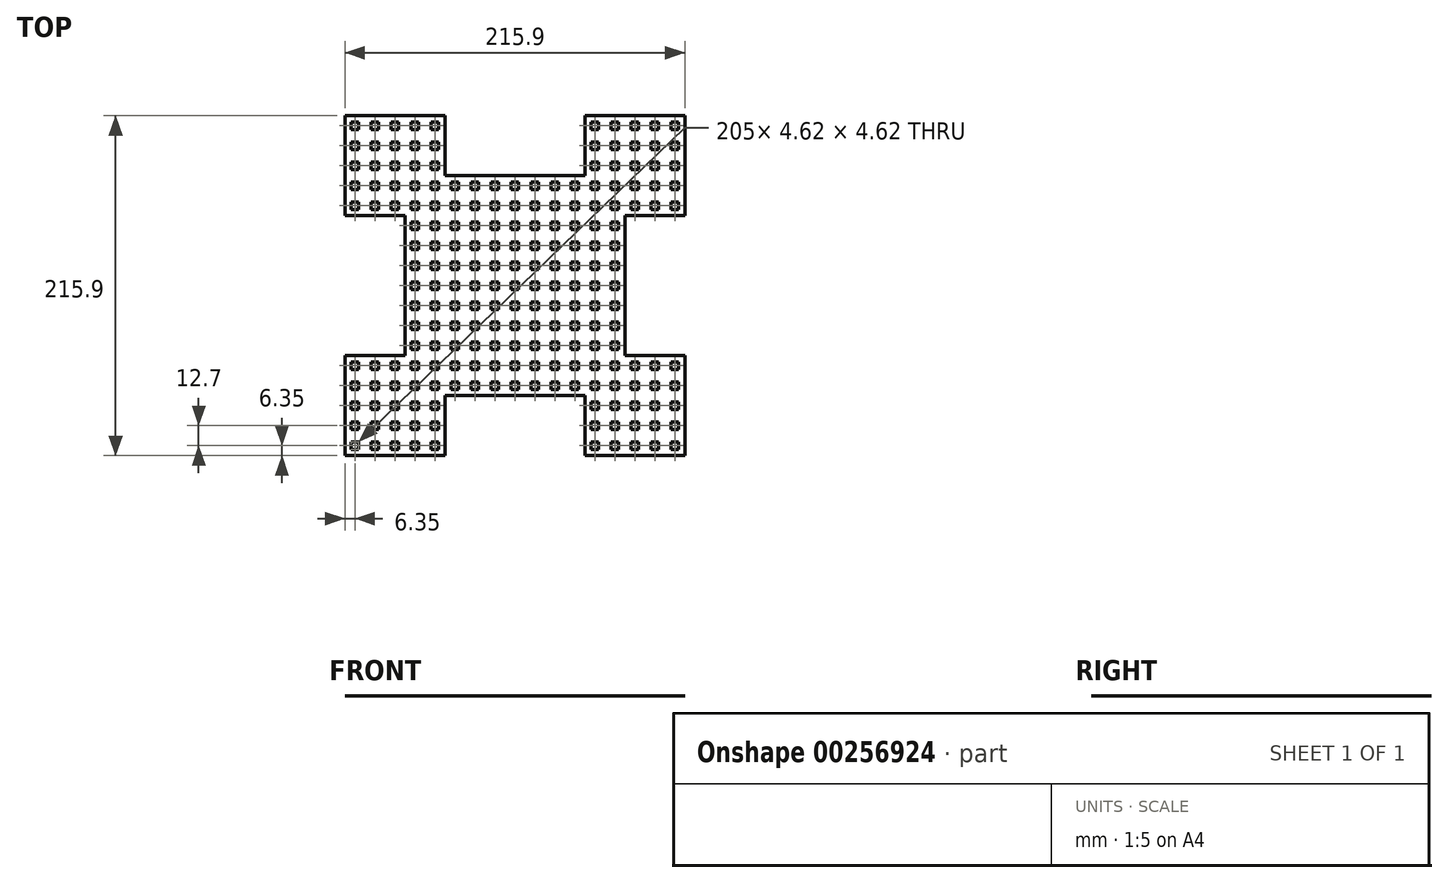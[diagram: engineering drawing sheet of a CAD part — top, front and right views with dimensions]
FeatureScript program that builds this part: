
annotation { "Feature Type Name" : "Feature", "Feature Type Description" : "" }
export const myFeature = defineFeature(function(context is Context, id is Id, definition is map)
    precondition{}
    {
        {
            var Q0;
            Q0=qCreatedBy(makeId("Top.planeOp"),FACE);
            var sketch = newSketch(context, id + "F0", { "sketchPlane" : qUnion([Q0])});
            skLineSegment(sketch, "E0.bottom", {"start": v(101.6, 101.6) * mm, "end": v(50.8, 101.6) * mm});
            skLineSegment(sketch, "E0.right", {"start": v(-101.6, 101.6) * mm, "end": v(-101.6, 95.25) * mm});
            skPoint(sketch, "E0.middle", {"position": v(0, 0) * mm});
            skLineSegment(sketch, "E1.bottom", {"start": v(-101.6, 101.6) * mm, "end": v(-95.25, 101.6) * mm});
            skLineSegment(sketch, "E2.bottom", {"start": v(-97.56, 97.56) * mm, "end": v(-92.94, 97.56) * mm});
            skLineSegment(sketch, "E2.top", {"start": v(-97.56, 92.94) * mm, "end": v(-92.94, 92.94) * mm});
            skLineSegment(sketch, "E2.left", {"start": v(-97.56, 97.56) * mm, "end": v(-97.56, 92.94) * mm});
            skLineSegment(sketch, "E2.right", {"start": v(-92.94, 97.56) * mm, "end": v(-92.94, 92.94) * mm});
            skPoint(sketch, "E2.middle", {"position": v(-95.25, 95.25) * mm});
            skLineSegment(sketch, "E3.0.1.0", {"start": v(-97.56, 84.86) * mm, "end": v(-92.94, 84.86) * mm});
            skLineSegment(sketch, "E3.0.1.1", {"start": v(-97.56, 84.86) * mm, "end": v(-97.56, 80.24) * mm});
            skLineSegment(sketch, "E3.0.1.2", {"start": v(-92.94, 84.86) * mm, "end": v(-92.94, 80.24) * mm});
            skLineSegment(sketch, "E3.0.1.3", {"start": v(-97.56, 80.24) * mm, "end": v(-92.94, 80.24) * mm});
            skLineSegment(sketch, "E3.0.2.0", {"start": v(-97.56, 72.16) * mm, "end": v(-92.94, 72.16) * mm});
            skLineSegment(sketch, "E3.0.2.1", {"start": v(-97.56, 72.16) * mm, "end": v(-97.56, 67.54) * mm});
            skLineSegment(sketch, "E3.0.2.2", {"start": v(-92.94, 72.16) * mm, "end": v(-92.94, 67.54) * mm});
            skLineSegment(sketch, "E3.0.2.3", {"start": v(-97.56, 67.54) * mm, "end": v(-92.94, 67.54) * mm});
            skLineSegment(sketch, "E3.0.3.0", {"start": v(-97.56, 59.46) * mm, "end": v(-92.94, 59.46) * mm});
            skLineSegment(sketch, "E3.0.3.1", {"start": v(-97.56, 59.46) * mm, "end": v(-97.56, 54.84) * mm});
            skLineSegment(sketch, "E3.0.3.2", {"start": v(-92.94, 59.46) * mm, "end": v(-92.94, 54.84) * mm});
            skLineSegment(sketch, "E3.0.3.3", {"start": v(-97.56, 54.84) * mm, "end": v(-92.94, 54.84) * mm});
            skLineSegment(sketch, "E3.0.4.0", {"start": v(-97.56, 46.76) * mm, "end": v(-92.94, 46.76) * mm});
            skLineSegment(sketch, "E3.0.4.1", {"start": v(-97.56, 46.76) * mm, "end": v(-97.56, 42.14) * mm});
            skLineSegment(sketch, "E3.0.4.2", {"start": v(-92.94, 46.76) * mm, "end": v(-92.94, 42.14) * mm});
            skLineSegment(sketch, "E3.0.4.3", {"start": v(-97.56, 42.14) * mm, "end": v(-92.94, 42.14) * mm});
            skLineSegment(sketch, "E3.0.5.0", {"start": v(-97.56, 34.06) * mm, "end": v(-92.94, 34.06) * mm});
            skLineSegment(sketch, "E3.0.5.1", {"start": v(-97.56, 34.06) * mm, "end": v(-97.56, 29.44) * mm});
            skLineSegment(sketch, "E3.0.5.2", {"start": v(-92.94, 34.06) * mm, "end": v(-92.94, 29.44) * mm});
            skLineSegment(sketch, "E3.0.5.3", {"start": v(-97.56, 29.44) * mm, "end": v(-92.94, 29.44) * mm});
            skLineSegment(sketch, "E3.0.6.0", {"start": v(-97.56, 21.36) * mm, "end": v(-92.94, 21.36) * mm});
            skLineSegment(sketch, "E3.0.6.1", {"start": v(-97.56, 21.36) * mm, "end": v(-97.56, 16.74) * mm});
            skLineSegment(sketch, "E3.0.6.2", {"start": v(-92.94, 21.36) * mm, "end": v(-92.94, 16.74) * mm});
            skLineSegment(sketch, "E3.0.6.3", {"start": v(-97.56, 16.74) * mm, "end": v(-92.94, 16.74) * mm});
            skLineSegment(sketch, "E3.0.7.0", {"start": v(-97.56, 8.66) * mm, "end": v(-92.94, 8.66) * mm});
            skLineSegment(sketch, "E3.0.7.1", {"start": v(-97.56, 8.66) * mm, "end": v(-97.56, 4.04) * mm});
            skLineSegment(sketch, "E3.0.7.2", {"start": v(-92.94, 8.66) * mm, "end": v(-92.94, 4.04) * mm});
            skLineSegment(sketch, "E3.0.7.3", {"start": v(-97.56, 4.04) * mm, "end": v(-92.94, 4.04) * mm});
            skLineSegment(sketch, "E3.0.8.0", {"start": v(-97.56, -4.04) * mm, "end": v(-92.94, -4.04) * mm});
            skLineSegment(sketch, "E3.0.8.1", {"start": v(-97.56, -4.04) * mm, "end": v(-97.56, -8.66) * mm});
            skLineSegment(sketch, "E3.0.8.2", {"start": v(-92.94, -4.04) * mm, "end": v(-92.94, -8.66) * mm});
            skLineSegment(sketch, "E3.0.8.3", {"start": v(-97.56, -8.66) * mm, "end": v(-92.94, -8.66) * mm});
            skLineSegment(sketch, "E3.0.9.0", {"start": v(-97.56, -16.74) * mm, "end": v(-92.94, -16.74) * mm});
            skLineSegment(sketch, "E3.0.9.1", {"start": v(-97.56, -16.74) * mm, "end": v(-97.56, -21.36) * mm});
            skLineSegment(sketch, "E3.0.9.2", {"start": v(-92.94, -16.74) * mm, "end": v(-92.94, -21.36) * mm});
            skLineSegment(sketch, "E3.0.9.3", {"start": v(-97.56, -21.36) * mm, "end": v(-92.94, -21.36) * mm});
            skLineSegment(sketch, "E3.0.10.0", {"start": v(-97.56, -29.44) * mm, "end": v(-92.94, -29.44) * mm});
            skLineSegment(sketch, "E3.0.10.1", {"start": v(-97.56, -29.44) * mm, "end": v(-97.56, -34.06) * mm});
            skLineSegment(sketch, "E3.0.10.2", {"start": v(-92.94, -29.44) * mm, "end": v(-92.94, -34.06) * mm});
            skLineSegment(sketch, "E3.0.10.3", {"start": v(-97.56, -34.06) * mm, "end": v(-92.94, -34.06) * mm});
            skLineSegment(sketch, "E3.0.11.0", {"start": v(-97.56, -42.14) * mm, "end": v(-92.94, -42.14) * mm});
            skLineSegment(sketch, "E3.0.11.1", {"start": v(-97.56, -42.14) * mm, "end": v(-97.56, -46.76) * mm});
            skLineSegment(sketch, "E3.0.11.2", {"start": v(-92.94, -42.14) * mm, "end": v(-92.94, -46.76) * mm});
            skLineSegment(sketch, "E3.0.11.3", {"start": v(-97.56, -46.76) * mm, "end": v(-92.94, -46.76) * mm});
            skLineSegment(sketch, "E3.0.12.0", {"start": v(-97.56, -54.84) * mm, "end": v(-92.94, -54.84) * mm});
            skLineSegment(sketch, "E3.0.12.1", {"start": v(-97.56, -54.84) * mm, "end": v(-97.56, -59.46) * mm});
            skLineSegment(sketch, "E3.0.12.2", {"start": v(-92.94, -54.84) * mm, "end": v(-92.94, -59.46) * mm});
            skLineSegment(sketch, "E3.0.12.3", {"start": v(-97.56, -59.46) * mm, "end": v(-92.94, -59.46) * mm});
            skLineSegment(sketch, "E3.0.13.0", {"start": v(-97.56, -67.54) * mm, "end": v(-92.94, -67.54) * mm});
            skLineSegment(sketch, "E3.0.13.1", {"start": v(-97.56, -67.54) * mm, "end": v(-97.56, -72.16) * mm});
            skLineSegment(sketch, "E3.0.13.2", {"start": v(-92.94, -67.54) * mm, "end": v(-92.94, -72.16) * mm});
            skLineSegment(sketch, "E3.0.13.3", {"start": v(-97.56, -72.16) * mm, "end": v(-92.94, -72.16) * mm});
            skLineSegment(sketch, "E3.0.14.0", {"start": v(-97.56, -80.24) * mm, "end": v(-92.94, -80.24) * mm});
            skLineSegment(sketch, "E3.0.14.1", {"start": v(-97.56, -80.24) * mm, "end": v(-97.56, -84.86) * mm});
            skLineSegment(sketch, "E3.0.14.2", {"start": v(-92.94, -80.24) * mm, "end": v(-92.94, -84.86) * mm});
            skLineSegment(sketch, "E3.0.14.3", {"start": v(-97.56, -84.86) * mm, "end": v(-92.94, -84.86) * mm});
            skLineSegment(sketch, "E3.0.15.0", {"start": v(-97.56, -92.94) * mm, "end": v(-92.94, -92.94) * mm});
            skLineSegment(sketch, "E3.0.15.1", {"start": v(-97.56, -92.94) * mm, "end": v(-97.56, -97.56) * mm});
            skLineSegment(sketch, "E3.0.15.2", {"start": v(-92.94, -92.94) * mm, "end": v(-92.94, -97.56) * mm});
            skLineSegment(sketch, "E3.0.15.3", {"start": v(-97.56, -97.56) * mm, "end": v(-92.94, -97.56) * mm});
            skLineSegment(sketch, "E3.0.16.0", {"start": v(-97.56, -105.64) * mm, "end": v(-92.94, -105.64) * mm});
            skLineSegment(sketch, "E3.0.16.1", {"start": v(-97.56, -105.64) * mm, "end": v(-97.56, -110.26) * mm});
            skLineSegment(sketch, "E3.0.16.2", {"start": v(-92.94, -105.64) * mm, "end": v(-92.94, -110.26) * mm});
            skLineSegment(sketch, "E3.0.16.3", {"start": v(-97.56, -110.26) * mm, "end": v(-92.94, -110.26) * mm});
            skLineSegment(sketch, "E3.1.0.0", {"start": v(-84.86, 97.56) * mm, "end": v(-80.24, 97.56) * mm});
            skLineSegment(sketch, "E3.1.0.1", {"start": v(-84.86, 97.56) * mm, "end": v(-84.86, 92.94) * mm});
            skLineSegment(sketch, "E3.1.0.2", {"start": v(-80.24, 97.56) * mm, "end": v(-80.24, 92.94) * mm});
            skLineSegment(sketch, "E3.1.0.3", {"start": v(-84.86, 92.94) * mm, "end": v(-80.24, 92.94) * mm});
            skLineSegment(sketch, "E3.1.1.0", {"start": v(-84.86, 84.86) * mm, "end": v(-80.24, 84.86) * mm});
            skLineSegment(sketch, "E3.1.1.1", {"start": v(-84.86, 84.86) * mm, "end": v(-84.86, 80.24) * mm});
            skLineSegment(sketch, "E3.1.1.2", {"start": v(-80.24, 84.86) * mm, "end": v(-80.24, 80.24) * mm});
            skLineSegment(sketch, "E3.1.1.3", {"start": v(-84.86, 80.24) * mm, "end": v(-80.24, 80.24) * mm});
            skLineSegment(sketch, "E3.1.2.0", {"start": v(-84.86, 72.16) * mm, "end": v(-80.24, 72.16) * mm});
            skLineSegment(sketch, "E3.1.2.1", {"start": v(-84.86, 72.16) * mm, "end": v(-84.86, 67.54) * mm});
            skLineSegment(sketch, "E3.1.2.2", {"start": v(-80.24, 72.16) * mm, "end": v(-80.24, 67.54) * mm});
            skLineSegment(sketch, "E3.1.2.3", {"start": v(-84.86, 67.54) * mm, "end": v(-80.24, 67.54) * mm});
            skLineSegment(sketch, "E3.1.3.0", {"start": v(-84.86, 59.46) * mm, "end": v(-80.24, 59.46) * mm});
            skLineSegment(sketch, "E3.1.3.1", {"start": v(-84.86, 59.46) * mm, "end": v(-84.86, 54.84) * mm});
            skLineSegment(sketch, "E3.1.3.2", {"start": v(-80.24, 59.46) * mm, "end": v(-80.24, 54.84) * mm});
            skLineSegment(sketch, "E3.1.3.3", {"start": v(-84.86, 54.84) * mm, "end": v(-80.24, 54.84) * mm});
            skLineSegment(sketch, "E3.1.4.0", {"start": v(-84.86, 46.76) * mm, "end": v(-80.24, 46.76) * mm});
            skLineSegment(sketch, "E3.1.4.1", {"start": v(-84.86, 46.76) * mm, "end": v(-84.86, 42.14) * mm});
            skLineSegment(sketch, "E3.1.4.2", {"start": v(-80.24, 46.76) * mm, "end": v(-80.24, 42.14) * mm});
            skLineSegment(sketch, "E3.1.4.3", {"start": v(-84.86, 42.14) * mm, "end": v(-80.24, 42.14) * mm});
            skLineSegment(sketch, "E3.1.5.0", {"start": v(-84.86, 34.06) * mm, "end": v(-80.24, 34.06) * mm});
            skLineSegment(sketch, "E3.1.5.1", {"start": v(-84.86, 34.06) * mm, "end": v(-84.86, 29.44) * mm});
            skLineSegment(sketch, "E3.1.5.2", {"start": v(-80.24, 34.06) * mm, "end": v(-80.24, 29.44) * mm});
            skLineSegment(sketch, "E3.1.5.3", {"start": v(-84.86, 29.44) * mm, "end": v(-80.24, 29.44) * mm});
            skLineSegment(sketch, "E3.1.6.0", {"start": v(-84.86, 21.36) * mm, "end": v(-80.24, 21.36) * mm});
            skLineSegment(sketch, "E3.1.6.1", {"start": v(-84.86, 21.36) * mm, "end": v(-84.86, 16.74) * mm});
            skLineSegment(sketch, "E3.1.6.2", {"start": v(-80.24, 21.36) * mm, "end": v(-80.24, 16.74) * mm});
            skLineSegment(sketch, "E3.1.6.3", {"start": v(-84.86, 16.74) * mm, "end": v(-80.24, 16.74) * mm});
            skLineSegment(sketch, "E3.1.7.0", {"start": v(-84.86, 8.66) * mm, "end": v(-80.24, 8.66) * mm});
            skLineSegment(sketch, "E3.1.7.1", {"start": v(-84.86, 8.66) * mm, "end": v(-84.86, 4.04) * mm});
            skLineSegment(sketch, "E3.1.7.2", {"start": v(-80.24, 8.66) * mm, "end": v(-80.24, 4.04) * mm});
            skLineSegment(sketch, "E3.1.7.3", {"start": v(-84.86, 4.04) * mm, "end": v(-80.24, 4.04) * mm});
            skLineSegment(sketch, "E3.1.8.0", {"start": v(-84.86, -4.04) * mm, "end": v(-80.24, -4.04) * mm});
            skLineSegment(sketch, "E3.1.8.1", {"start": v(-84.86, -4.04) * mm, "end": v(-84.86, -8.66) * mm});
            skLineSegment(sketch, "E3.1.8.2", {"start": v(-80.24, -4.04) * mm, "end": v(-80.24, -8.66) * mm});
            skLineSegment(sketch, "E3.1.8.3", {"start": v(-84.86, -8.66) * mm, "end": v(-80.24, -8.66) * mm});
            skLineSegment(sketch, "E3.1.9.0", {"start": v(-84.86, -16.74) * mm, "end": v(-80.24, -16.74) * mm});
            skLineSegment(sketch, "E3.1.9.1", {"start": v(-84.86, -16.74) * mm, "end": v(-84.86, -21.36) * mm});
            skLineSegment(sketch, "E3.1.9.2", {"start": v(-80.24, -16.74) * mm, "end": v(-80.24, -21.36) * mm});
            skLineSegment(sketch, "E3.1.9.3", {"start": v(-84.86, -21.36) * mm, "end": v(-80.24, -21.36) * mm});
            skLineSegment(sketch, "E3.1.10.0", {"start": v(-84.86, -29.44) * mm, "end": v(-80.24, -29.44) * mm});
            skLineSegment(sketch, "E3.1.10.1", {"start": v(-84.86, -29.44) * mm, "end": v(-84.86, -34.06) * mm});
            skLineSegment(sketch, "E3.1.10.2", {"start": v(-80.24, -29.44) * mm, "end": v(-80.24, -34.06) * mm});
            skLineSegment(sketch, "E3.1.10.3", {"start": v(-84.86, -34.06) * mm, "end": v(-80.24, -34.06) * mm});
            skLineSegment(sketch, "E3.1.11.0", {"start": v(-84.86, -42.14) * mm, "end": v(-80.24, -42.14) * mm});
            skLineSegment(sketch, "E3.1.11.1", {"start": v(-84.86, -42.14) * mm, "end": v(-84.86, -46.76) * mm});
            skLineSegment(sketch, "E3.1.11.2", {"start": v(-80.24, -42.14) * mm, "end": v(-80.24, -46.76) * mm});
            skLineSegment(sketch, "E3.1.11.3", {"start": v(-84.86, -46.76) * mm, "end": v(-80.24, -46.76) * mm});
            skLineSegment(sketch, "E3.1.12.0", {"start": v(-84.86, -54.84) * mm, "end": v(-80.24, -54.84) * mm});
            skLineSegment(sketch, "E3.1.12.1", {"start": v(-84.86, -54.84) * mm, "end": v(-84.86, -59.46) * mm});
            skLineSegment(sketch, "E3.1.12.2", {"start": v(-80.24, -54.84) * mm, "end": v(-80.24, -59.46) * mm});
            skLineSegment(sketch, "E3.1.12.3", {"start": v(-84.86, -59.46) * mm, "end": v(-80.24, -59.46) * mm});
            skLineSegment(sketch, "E3.1.13.0", {"start": v(-84.86, -67.54) * mm, "end": v(-80.24, -67.54) * mm});
            skLineSegment(sketch, "E3.1.13.1", {"start": v(-84.86, -67.54) * mm, "end": v(-84.86, -72.16) * mm});
            skLineSegment(sketch, "E3.1.13.2", {"start": v(-80.24, -67.54) * mm, "end": v(-80.24, -72.16) * mm});
            skLineSegment(sketch, "E3.1.13.3", {"start": v(-84.86, -72.16) * mm, "end": v(-80.24, -72.16) * mm});
            skLineSegment(sketch, "E3.1.14.0", {"start": v(-84.86, -80.24) * mm, "end": v(-80.24, -80.24) * mm});
            skLineSegment(sketch, "E3.1.14.1", {"start": v(-84.86, -80.24) * mm, "end": v(-84.86, -84.86) * mm});
            skLineSegment(sketch, "E3.1.14.2", {"start": v(-80.24, -80.24) * mm, "end": v(-80.24, -84.86) * mm});
            skLineSegment(sketch, "E3.1.14.3", {"start": v(-84.86, -84.86) * mm, "end": v(-80.24, -84.86) * mm});
            skLineSegment(sketch, "E3.1.15.0", {"start": v(-84.86, -92.94) * mm, "end": v(-80.24, -92.94) * mm});
            skLineSegment(sketch, "E3.1.15.1", {"start": v(-84.86, -92.94) * mm, "end": v(-84.86, -97.56) * mm});
            skLineSegment(sketch, "E3.1.15.2", {"start": v(-80.24, -92.94) * mm, "end": v(-80.24, -97.56) * mm});
            skLineSegment(sketch, "E3.1.15.3", {"start": v(-84.86, -97.56) * mm, "end": v(-80.24, -97.56) * mm});
            skLineSegment(sketch, "E3.1.16.0", {"start": v(-84.86, -105.64) * mm, "end": v(-80.24, -105.64) * mm});
            skLineSegment(sketch, "E3.1.16.1", {"start": v(-84.86, -105.64) * mm, "end": v(-84.86, -110.26) * mm});
            skLineSegment(sketch, "E3.1.16.2", {"start": v(-80.24, -105.64) * mm, "end": v(-80.24, -110.26) * mm});
            skLineSegment(sketch, "E3.1.16.3", {"start": v(-84.86, -110.26) * mm, "end": v(-80.24, -110.26) * mm});
            skLineSegment(sketch, "E3.2.0.0", {"start": v(-72.16, 97.56) * mm, "end": v(-67.54, 97.56) * mm});
            skLineSegment(sketch, "E3.2.0.1", {"start": v(-72.16, 97.56) * mm, "end": v(-72.16, 92.94) * mm});
            skLineSegment(sketch, "E3.2.0.2", {"start": v(-67.54, 97.56) * mm, "end": v(-67.54, 92.94) * mm});
            skLineSegment(sketch, "E3.2.0.3", {"start": v(-72.16, 92.94) * mm, "end": v(-67.54, 92.94) * mm});
            skLineSegment(sketch, "E3.2.1.0", {"start": v(-72.16, 84.86) * mm, "end": v(-67.54, 84.86) * mm});
            skLineSegment(sketch, "E3.2.1.1", {"start": v(-72.16, 84.86) * mm, "end": v(-72.16, 80.24) * mm});
            skLineSegment(sketch, "E3.2.1.2", {"start": v(-67.54, 84.86) * mm, "end": v(-67.54, 80.24) * mm});
            skLineSegment(sketch, "E3.2.1.3", {"start": v(-72.16, 80.24) * mm, "end": v(-67.54, 80.24) * mm});
            skLineSegment(sketch, "E3.2.2.0", {"start": v(-72.16, 72.16) * mm, "end": v(-67.54, 72.16) * mm});
            skLineSegment(sketch, "E3.2.2.1", {"start": v(-72.16, 72.16) * mm, "end": v(-72.16, 67.54) * mm});
            skLineSegment(sketch, "E3.2.2.2", {"start": v(-67.54, 72.16) * mm, "end": v(-67.54, 67.54) * mm});
            skLineSegment(sketch, "E3.2.2.3", {"start": v(-72.16, 67.54) * mm, "end": v(-67.54, 67.54) * mm});
            skLineSegment(sketch, "E3.2.3.0", {"start": v(-72.16, 59.46) * mm, "end": v(-67.54, 59.46) * mm});
            skLineSegment(sketch, "E3.2.3.1", {"start": v(-72.16, 59.46) * mm, "end": v(-72.16, 54.84) * mm});
            skLineSegment(sketch, "E3.2.3.2", {"start": v(-67.54, 59.46) * mm, "end": v(-67.54, 54.84) * mm});
            skLineSegment(sketch, "E3.2.3.3", {"start": v(-72.16, 54.84) * mm, "end": v(-67.54, 54.84) * mm});
            skLineSegment(sketch, "E3.2.4.0", {"start": v(-72.16, 46.76) * mm, "end": v(-67.54, 46.76) * mm});
            skLineSegment(sketch, "E3.2.4.1", {"start": v(-72.16, 46.76) * mm, "end": v(-72.16, 42.14) * mm});
            skLineSegment(sketch, "E3.2.4.2", {"start": v(-67.54, 46.76) * mm, "end": v(-67.54, 42.14) * mm});
            skLineSegment(sketch, "E3.2.4.3", {"start": v(-72.16, 42.14) * mm, "end": v(-67.54, 42.14) * mm});
            skLineSegment(sketch, "E3.2.5.0", {"start": v(-72.16, 34.06) * mm, "end": v(-67.54, 34.06) * mm});
            skLineSegment(sketch, "E3.2.5.1", {"start": v(-72.16, 34.06) * mm, "end": v(-72.16, 29.44) * mm});
            skLineSegment(sketch, "E3.2.5.2", {"start": v(-67.54, 34.06) * mm, "end": v(-67.54, 29.44) * mm});
            skLineSegment(sketch, "E3.2.5.3", {"start": v(-72.16, 29.44) * mm, "end": v(-67.54, 29.44) * mm});
            skLineSegment(sketch, "E3.2.6.0", {"start": v(-72.16, 21.36) * mm, "end": v(-67.54, 21.36) * mm});
            skLineSegment(sketch, "E3.2.6.1", {"start": v(-72.16, 21.36) * mm, "end": v(-72.16, 16.74) * mm});
            skLineSegment(sketch, "E3.2.6.2", {"start": v(-67.54, 21.36) * mm, "end": v(-67.54, 16.74) * mm});
            skLineSegment(sketch, "E3.2.6.3", {"start": v(-72.16, 16.74) * mm, "end": v(-67.54, 16.74) * mm});
            skLineSegment(sketch, "E3.2.7.0", {"start": v(-72.16, 8.66) * mm, "end": v(-67.54, 8.66) * mm});
            skLineSegment(sketch, "E3.2.7.1", {"start": v(-72.16, 8.66) * mm, "end": v(-72.16, 4.04) * mm});
            skLineSegment(sketch, "E3.2.7.2", {"start": v(-67.54, 8.66) * mm, "end": v(-67.54, 4.04) * mm});
            skLineSegment(sketch, "E3.2.7.3", {"start": v(-72.16, 4.04) * mm, "end": v(-67.54, 4.04) * mm});
            skLineSegment(sketch, "E3.2.8.0", {"start": v(-72.16, -4.04) * mm, "end": v(-67.54, -4.04) * mm});
            skLineSegment(sketch, "E3.2.8.1", {"start": v(-72.16, -4.04) * mm, "end": v(-72.16, -8.66) * mm});
            skLineSegment(sketch, "E3.2.8.2", {"start": v(-67.54, -4.04) * mm, "end": v(-67.54, -8.66) * mm});
            skLineSegment(sketch, "E3.2.8.3", {"start": v(-72.16, -8.66) * mm, "end": v(-67.54, -8.66) * mm});
            skLineSegment(sketch, "E3.2.9.0", {"start": v(-72.16, -16.74) * mm, "end": v(-67.54, -16.74) * mm});
            skLineSegment(sketch, "E3.2.9.1", {"start": v(-72.16, -16.74) * mm, "end": v(-72.16, -21.36) * mm});
            skLineSegment(sketch, "E3.2.9.2", {"start": v(-67.54, -16.74) * mm, "end": v(-67.54, -21.36) * mm});
            skLineSegment(sketch, "E3.2.9.3", {"start": v(-72.16, -21.36) * mm, "end": v(-67.54, -21.36) * mm});
            skLineSegment(sketch, "E3.2.10.0", {"start": v(-72.16, -29.44) * mm, "end": v(-67.54, -29.44) * mm});
            skLineSegment(sketch, "E3.2.10.1", {"start": v(-72.16, -29.44) * mm, "end": v(-72.16, -34.06) * mm});
            skLineSegment(sketch, "E3.2.10.2", {"start": v(-67.54, -29.44) * mm, "end": v(-67.54, -34.06) * mm});
            skLineSegment(sketch, "E3.2.10.3", {"start": v(-72.16, -34.06) * mm, "end": v(-67.54, -34.06) * mm});
            skLineSegment(sketch, "E3.2.11.0", {"start": v(-72.16, -42.14) * mm, "end": v(-67.54, -42.14) * mm});
            skLineSegment(sketch, "E3.2.11.1", {"start": v(-72.16, -42.14) * mm, "end": v(-72.16, -46.76) * mm});
            skLineSegment(sketch, "E3.2.11.2", {"start": v(-67.54, -42.14) * mm, "end": v(-67.54, -46.76) * mm});
            skLineSegment(sketch, "E3.2.11.3", {"start": v(-72.16, -46.76) * mm, "end": v(-67.54, -46.76) * mm});
            skLineSegment(sketch, "E3.2.12.0", {"start": v(-72.16, -54.84) * mm, "end": v(-67.54, -54.84) * mm});
            skLineSegment(sketch, "E3.2.12.1", {"start": v(-72.16, -54.84) * mm, "end": v(-72.16, -59.46) * mm});
            skLineSegment(sketch, "E3.2.12.2", {"start": v(-67.54, -54.84) * mm, "end": v(-67.54, -59.46) * mm});
            skLineSegment(sketch, "E3.2.12.3", {"start": v(-72.16, -59.46) * mm, "end": v(-67.54, -59.46) * mm});
            skLineSegment(sketch, "E3.2.13.0", {"start": v(-72.16, -67.54) * mm, "end": v(-67.54, -67.54) * mm});
            skLineSegment(sketch, "E3.2.13.1", {"start": v(-72.16, -67.54) * mm, "end": v(-72.16, -72.16) * mm});
            skLineSegment(sketch, "E3.2.13.2", {"start": v(-67.54, -67.54) * mm, "end": v(-67.54, -72.16) * mm});
            skLineSegment(sketch, "E3.2.13.3", {"start": v(-72.16, -72.16) * mm, "end": v(-67.54, -72.16) * mm});
            skLineSegment(sketch, "E3.2.14.0", {"start": v(-72.16, -80.24) * mm, "end": v(-67.54, -80.24) * mm});
            skLineSegment(sketch, "E3.2.14.1", {"start": v(-72.16, -80.24) * mm, "end": v(-72.16, -84.86) * mm});
            skLineSegment(sketch, "E3.2.14.2", {"start": v(-67.54, -80.24) * mm, "end": v(-67.54, -84.86) * mm});
            skLineSegment(sketch, "E3.2.14.3", {"start": v(-72.16, -84.86) * mm, "end": v(-67.54, -84.86) * mm});
            skLineSegment(sketch, "E3.2.15.0", {"start": v(-72.16, -92.94) * mm, "end": v(-67.54, -92.94) * mm});
            skLineSegment(sketch, "E3.2.15.1", {"start": v(-72.16, -92.94) * mm, "end": v(-72.16, -97.56) * mm});
            skLineSegment(sketch, "E3.2.15.2", {"start": v(-67.54, -92.94) * mm, "end": v(-67.54, -97.56) * mm});
            skLineSegment(sketch, "E3.2.15.3", {"start": v(-72.16, -97.56) * mm, "end": v(-67.54, -97.56) * mm});
            skLineSegment(sketch, "E3.2.16.0", {"start": v(-72.16, -105.64) * mm, "end": v(-67.54, -105.64) * mm});
            skLineSegment(sketch, "E3.2.16.1", {"start": v(-72.16, -105.64) * mm, "end": v(-72.16, -110.26) * mm});
            skLineSegment(sketch, "E3.2.16.2", {"start": v(-67.54, -105.64) * mm, "end": v(-67.54, -110.26) * mm});
            skLineSegment(sketch, "E3.2.16.3", {"start": v(-72.16, -110.26) * mm, "end": v(-67.54, -110.26) * mm});
            skLineSegment(sketch, "E3.3.0.0", {"start": v(-59.46, 97.56) * mm, "end": v(-54.84, 97.56) * mm});
            skLineSegment(sketch, "E3.3.0.1", {"start": v(-59.46, 97.56) * mm, "end": v(-59.46, 92.94) * mm});
            skLineSegment(sketch, "E3.3.0.2", {"start": v(-54.84, 97.56) * mm, "end": v(-54.84, 92.94) * mm});
            skLineSegment(sketch, "E3.3.0.3", {"start": v(-59.46, 92.94) * mm, "end": v(-54.84, 92.94) * mm});
            skLineSegment(sketch, "E3.3.1.0", {"start": v(-59.46, 84.86) * mm, "end": v(-54.84, 84.86) * mm});
            skLineSegment(sketch, "E3.3.1.1", {"start": v(-59.46, 84.86) * mm, "end": v(-59.46, 80.24) * mm});
            skLineSegment(sketch, "E3.3.1.2", {"start": v(-54.84, 84.86) * mm, "end": v(-54.84, 80.24) * mm});
            skLineSegment(sketch, "E3.3.1.3", {"start": v(-59.46, 80.24) * mm, "end": v(-54.84, 80.24) * mm});
            skLineSegment(sketch, "E3.3.2.0", {"start": v(-59.46, 72.16) * mm, "end": v(-54.84, 72.16) * mm});
            skLineSegment(sketch, "E3.3.2.1", {"start": v(-59.46, 72.16) * mm, "end": v(-59.46, 67.54) * mm});
            skLineSegment(sketch, "E3.3.2.2", {"start": v(-54.84, 72.16) * mm, "end": v(-54.84, 67.54) * mm});
            skLineSegment(sketch, "E3.3.2.3", {"start": v(-59.46, 67.54) * mm, "end": v(-54.84, 67.54) * mm});
            skLineSegment(sketch, "E3.3.3.0", {"start": v(-59.46, 59.46) * mm, "end": v(-54.84, 59.46) * mm});
            skLineSegment(sketch, "E3.3.3.1", {"start": v(-59.46, 59.46) * mm, "end": v(-59.46, 54.84) * mm});
            skLineSegment(sketch, "E3.3.3.2", {"start": v(-54.84, 59.46) * mm, "end": v(-54.84, 54.84) * mm});
            skLineSegment(sketch, "E3.3.3.3", {"start": v(-59.46, 54.84) * mm, "end": v(-54.84, 54.84) * mm});
            skLineSegment(sketch, "E3.3.4.0", {"start": v(-59.46, 46.76) * mm, "end": v(-54.84, 46.76) * mm});
            skLineSegment(sketch, "E3.3.4.1", {"start": v(-59.46, 46.76) * mm, "end": v(-59.46, 42.14) * mm});
            skLineSegment(sketch, "E3.3.4.2", {"start": v(-54.84, 46.76) * mm, "end": v(-54.84, 42.14) * mm});
            skLineSegment(sketch, "E3.3.4.3", {"start": v(-59.46, 42.14) * mm, "end": v(-54.84, 42.14) * mm});
            skLineSegment(sketch, "E3.3.5.0", {"start": v(-59.46, 34.06) * mm, "end": v(-54.84, 34.06) * mm});
            skLineSegment(sketch, "E3.3.5.1", {"start": v(-59.46, 34.06) * mm, "end": v(-59.46, 29.44) * mm});
            skLineSegment(sketch, "E3.3.5.2", {"start": v(-54.84, 34.06) * mm, "end": v(-54.84, 29.44) * mm});
            skLineSegment(sketch, "E3.3.5.3", {"start": v(-59.46, 29.44) * mm, "end": v(-54.84, 29.44) * mm});
            skLineSegment(sketch, "E3.3.6.0", {"start": v(-59.46, 21.36) * mm, "end": v(-54.84, 21.36) * mm});
            skLineSegment(sketch, "E3.3.6.1", {"start": v(-59.46, 21.36) * mm, "end": v(-59.46, 16.74) * mm});
            skLineSegment(sketch, "E3.3.6.2", {"start": v(-54.84, 21.36) * mm, "end": v(-54.84, 16.74) * mm});
            skLineSegment(sketch, "E3.3.6.3", {"start": v(-59.46, 16.74) * mm, "end": v(-54.84, 16.74) * mm});
            skLineSegment(sketch, "E3.3.7.0", {"start": v(-59.46, 8.66) * mm, "end": v(-54.84, 8.66) * mm});
            skLineSegment(sketch, "E3.3.7.1", {"start": v(-59.46, 8.66) * mm, "end": v(-59.46, 4.04) * mm});
            skLineSegment(sketch, "E3.3.7.2", {"start": v(-54.84, 8.66) * mm, "end": v(-54.84, 4.04) * mm});
            skLineSegment(sketch, "E3.3.7.3", {"start": v(-59.46, 4.04) * mm, "end": v(-54.84, 4.04) * mm});
            skLineSegment(sketch, "E3.3.8.0", {"start": v(-59.46, -4.04) * mm, "end": v(-54.84, -4.04) * mm});
            skLineSegment(sketch, "E3.3.8.1", {"start": v(-59.46, -4.04) * mm, "end": v(-59.46, -8.66) * mm});
            skLineSegment(sketch, "E3.3.8.2", {"start": v(-54.84, -4.04) * mm, "end": v(-54.84, -8.66) * mm});
            skLineSegment(sketch, "E3.3.8.3", {"start": v(-59.46, -8.66) * mm, "end": v(-54.84, -8.66) * mm});
            skLineSegment(sketch, "E3.3.9.0", {"start": v(-59.46, -16.74) * mm, "end": v(-54.84, -16.74) * mm});
            skLineSegment(sketch, "E3.3.9.1", {"start": v(-59.46, -16.74) * mm, "end": v(-59.46, -21.36) * mm});
            skLineSegment(sketch, "E3.3.9.2", {"start": v(-54.84, -16.74) * mm, "end": v(-54.84, -21.36) * mm});
            skLineSegment(sketch, "E3.3.9.3", {"start": v(-59.46, -21.36) * mm, "end": v(-54.84, -21.36) * mm});
            skLineSegment(sketch, "E3.3.10.0", {"start": v(-59.46, -29.44) * mm, "end": v(-54.84, -29.44) * mm});
            skLineSegment(sketch, "E3.3.10.1", {"start": v(-59.46, -29.44) * mm, "end": v(-59.46, -34.06) * mm});
            skLineSegment(sketch, "E3.3.10.2", {"start": v(-54.84, -29.44) * mm, "end": v(-54.84, -34.06) * mm});
            skLineSegment(sketch, "E3.3.10.3", {"start": v(-59.46, -34.06) * mm, "end": v(-54.84, -34.06) * mm});
            skLineSegment(sketch, "E3.3.11.0", {"start": v(-59.46, -42.14) * mm, "end": v(-54.84, -42.14) * mm});
            skLineSegment(sketch, "E3.3.11.1", {"start": v(-59.46, -42.14) * mm, "end": v(-59.46, -46.76) * mm});
            skLineSegment(sketch, "E3.3.11.2", {"start": v(-54.84, -42.14) * mm, "end": v(-54.84, -46.76) * mm});
            skLineSegment(sketch, "E3.3.11.3", {"start": v(-59.46, -46.76) * mm, "end": v(-54.84, -46.76) * mm});
            skLineSegment(sketch, "E3.3.12.0", {"start": v(-59.46, -54.84) * mm, "end": v(-54.84, -54.84) * mm});
            skLineSegment(sketch, "E3.3.12.1", {"start": v(-59.46, -54.84) * mm, "end": v(-59.46, -59.46) * mm});
            skLineSegment(sketch, "E3.3.12.2", {"start": v(-54.84, -54.84) * mm, "end": v(-54.84, -59.46) * mm});
            skLineSegment(sketch, "E3.3.12.3", {"start": v(-59.46, -59.46) * mm, "end": v(-54.84, -59.46) * mm});
            skLineSegment(sketch, "E3.3.13.0", {"start": v(-59.46, -67.54) * mm, "end": v(-54.84, -67.54) * mm});
            skLineSegment(sketch, "E3.3.13.1", {"start": v(-59.46, -67.54) * mm, "end": v(-59.46, -72.16) * mm});
            skLineSegment(sketch, "E3.3.13.2", {"start": v(-54.84, -67.54) * mm, "end": v(-54.84, -72.16) * mm});
            skLineSegment(sketch, "E3.3.13.3", {"start": v(-59.46, -72.16) * mm, "end": v(-54.84, -72.16) * mm});
            skLineSegment(sketch, "E3.3.14.0", {"start": v(-59.46, -80.24) * mm, "end": v(-54.84, -80.24) * mm});
            skLineSegment(sketch, "E3.3.14.1", {"start": v(-59.46, -80.24) * mm, "end": v(-59.46, -84.86) * mm});
            skLineSegment(sketch, "E3.3.14.2", {"start": v(-54.84, -80.24) * mm, "end": v(-54.84, -84.86) * mm});
            skLineSegment(sketch, "E3.3.14.3", {"start": v(-59.46, -84.86) * mm, "end": v(-54.84, -84.86) * mm});
            skLineSegment(sketch, "E3.3.15.0", {"start": v(-59.46, -92.94) * mm, "end": v(-54.84, -92.94) * mm});
            skLineSegment(sketch, "E3.3.15.1", {"start": v(-59.46, -92.94) * mm, "end": v(-59.46, -97.56) * mm});
            skLineSegment(sketch, "E3.3.15.2", {"start": v(-54.84, -92.94) * mm, "end": v(-54.84, -97.56) * mm});
            skLineSegment(sketch, "E3.3.15.3", {"start": v(-59.46, -97.56) * mm, "end": v(-54.84, -97.56) * mm});
            skLineSegment(sketch, "E3.3.16.0", {"start": v(-59.46, -105.64) * mm, "end": v(-54.84, -105.64) * mm});
            skLineSegment(sketch, "E3.3.16.1", {"start": v(-59.46, -105.64) * mm, "end": v(-59.46, -110.26) * mm});
            skLineSegment(sketch, "E3.3.16.2", {"start": v(-54.84, -105.64) * mm, "end": v(-54.84, -110.26) * mm});
            skLineSegment(sketch, "E3.3.16.3", {"start": v(-59.46, -110.26) * mm, "end": v(-54.84, -110.26) * mm});
            skLineSegment(sketch, "E3.4.0.0", {"start": v(-46.76, 97.56) * mm, "end": v(-42.14, 97.56) * mm});
            skLineSegment(sketch, "E3.4.0.1", {"start": v(-46.76, 97.56) * mm, "end": v(-46.76, 92.94) * mm});
            skLineSegment(sketch, "E3.4.0.2", {"start": v(-42.14, 97.56) * mm, "end": v(-42.14, 92.94) * mm});
            skLineSegment(sketch, "E3.4.0.3", {"start": v(-46.76, 92.94) * mm, "end": v(-42.14, 92.94) * mm});
            skLineSegment(sketch, "E3.4.1.0", {"start": v(-46.76, 84.86) * mm, "end": v(-42.14, 84.86) * mm});
            skLineSegment(sketch, "E3.4.1.1", {"start": v(-46.76, 84.86) * mm, "end": v(-46.76, 80.24) * mm});
            skLineSegment(sketch, "E3.4.1.2", {"start": v(-42.14, 84.86) * mm, "end": v(-42.14, 80.24) * mm});
            skLineSegment(sketch, "E3.4.1.3", {"start": v(-46.76, 80.24) * mm, "end": v(-42.14, 80.24) * mm});
            skLineSegment(sketch, "E3.4.2.0", {"start": v(-46.76, 72.16) * mm, "end": v(-42.14, 72.16) * mm});
            skLineSegment(sketch, "E3.4.2.1", {"start": v(-46.76, 72.16) * mm, "end": v(-46.76, 67.54) * mm});
            skLineSegment(sketch, "E3.4.2.2", {"start": v(-42.14, 72.16) * mm, "end": v(-42.14, 67.54) * mm});
            skLineSegment(sketch, "E3.4.2.3", {"start": v(-46.76, 67.54) * mm, "end": v(-42.14, 67.54) * mm});
            skLineSegment(sketch, "E3.4.3.0", {"start": v(-46.76, 59.46) * mm, "end": v(-42.14, 59.46) * mm});
            skLineSegment(sketch, "E3.4.3.1", {"start": v(-46.76, 59.46) * mm, "end": v(-46.76, 54.84) * mm});
            skLineSegment(sketch, "E3.4.3.2", {"start": v(-42.14, 59.46) * mm, "end": v(-42.14, 54.84) * mm});
            skLineSegment(sketch, "E3.4.3.3", {"start": v(-46.76, 54.84) * mm, "end": v(-42.14, 54.84) * mm});
            skLineSegment(sketch, "E3.4.4.0", {"start": v(-46.76, 46.76) * mm, "end": v(-42.14, 46.76) * mm});
            skLineSegment(sketch, "E3.4.4.1", {"start": v(-46.76, 46.76) * mm, "end": v(-46.76, 42.14) * mm});
            skLineSegment(sketch, "E3.4.4.2", {"start": v(-42.14, 46.76) * mm, "end": v(-42.14, 42.14) * mm});
            skLineSegment(sketch, "E3.4.4.3", {"start": v(-46.76, 42.14) * mm, "end": v(-42.14, 42.14) * mm});
            skLineSegment(sketch, "E3.4.5.0", {"start": v(-46.76, 34.06) * mm, "end": v(-42.14, 34.06) * mm});
            skLineSegment(sketch, "E3.4.5.1", {"start": v(-46.76, 34.06) * mm, "end": v(-46.76, 29.44) * mm});
            skLineSegment(sketch, "E3.4.5.2", {"start": v(-42.14, 34.06) * mm, "end": v(-42.14, 29.44) * mm});
            skLineSegment(sketch, "E3.4.5.3", {"start": v(-46.76, 29.44) * mm, "end": v(-42.14, 29.44) * mm});
            skLineSegment(sketch, "E3.4.6.0", {"start": v(-46.76, 21.36) * mm, "end": v(-42.14, 21.36) * mm});
            skLineSegment(sketch, "E3.4.6.1", {"start": v(-46.76, 21.36) * mm, "end": v(-46.76, 16.74) * mm});
            skLineSegment(sketch, "E3.4.6.2", {"start": v(-42.14, 21.36) * mm, "end": v(-42.14, 16.74) * mm});
            skLineSegment(sketch, "E3.4.6.3", {"start": v(-46.76, 16.74) * mm, "end": v(-42.14, 16.74) * mm});
            skLineSegment(sketch, "E3.4.7.0", {"start": v(-46.76, 8.66) * mm, "end": v(-42.14, 8.66) * mm});
            skLineSegment(sketch, "E3.4.7.1", {"start": v(-46.76, 8.66) * mm, "end": v(-46.76, 4.04) * mm});
            skLineSegment(sketch, "E3.4.7.2", {"start": v(-42.14, 8.66) * mm, "end": v(-42.14, 4.04) * mm});
            skLineSegment(sketch, "E3.4.7.3", {"start": v(-46.76, 4.04) * mm, "end": v(-42.14, 4.04) * mm});
            skLineSegment(sketch, "E3.4.8.0", {"start": v(-46.76, -4.04) * mm, "end": v(-42.14, -4.04) * mm});
            skLineSegment(sketch, "E3.4.8.1", {"start": v(-46.76, -4.04) * mm, "end": v(-46.76, -8.66) * mm});
            skLineSegment(sketch, "E3.4.8.2", {"start": v(-42.14, -4.04) * mm, "end": v(-42.14, -8.66) * mm});
            skLineSegment(sketch, "E3.4.8.3", {"start": v(-46.76, -8.66) * mm, "end": v(-42.14, -8.66) * mm});
            skLineSegment(sketch, "E3.4.9.0", {"start": v(-46.76, -16.74) * mm, "end": v(-42.14, -16.74) * mm});
            skLineSegment(sketch, "E3.4.9.1", {"start": v(-46.76, -16.74) * mm, "end": v(-46.76, -21.36) * mm});
            skLineSegment(sketch, "E3.4.9.2", {"start": v(-42.14, -16.74) * mm, "end": v(-42.14, -21.36) * mm});
            skLineSegment(sketch, "E3.4.9.3", {"start": v(-46.76, -21.36) * mm, "end": v(-42.14, -21.36) * mm});
            skLineSegment(sketch, "E3.4.10.0", {"start": v(-46.76, -29.44) * mm, "end": v(-42.14, -29.44) * mm});
            skLineSegment(sketch, "E3.4.10.1", {"start": v(-46.76, -29.44) * mm, "end": v(-46.76, -34.06) * mm});
            skLineSegment(sketch, "E3.4.10.2", {"start": v(-42.14, -29.44) * mm, "end": v(-42.14, -34.06) * mm});
            skLineSegment(sketch, "E3.4.10.3", {"start": v(-46.76, -34.06) * mm, "end": v(-42.14, -34.06) * mm});
            skLineSegment(sketch, "E3.4.11.0", {"start": v(-46.76, -42.14) * mm, "end": v(-42.14, -42.14) * mm});
            skLineSegment(sketch, "E3.4.11.1", {"start": v(-46.76, -42.14) * mm, "end": v(-46.76, -46.76) * mm});
            skLineSegment(sketch, "E3.4.11.2", {"start": v(-42.14, -42.14) * mm, "end": v(-42.14, -46.76) * mm});
            skLineSegment(sketch, "E3.4.11.3", {"start": v(-46.76, -46.76) * mm, "end": v(-42.14, -46.76) * mm});
            skLineSegment(sketch, "E3.4.12.0", {"start": v(-46.76, -54.84) * mm, "end": v(-42.14, -54.84) * mm});
            skLineSegment(sketch, "E3.4.12.1", {"start": v(-46.76, -54.84) * mm, "end": v(-46.76, -59.46) * mm});
            skLineSegment(sketch, "E3.4.12.2", {"start": v(-42.14, -54.84) * mm, "end": v(-42.14, -59.46) * mm});
            skLineSegment(sketch, "E3.4.12.3", {"start": v(-46.76, -59.46) * mm, "end": v(-42.14, -59.46) * mm});
            skLineSegment(sketch, "E3.4.13.0", {"start": v(-46.76, -67.54) * mm, "end": v(-42.14, -67.54) * mm});
            skLineSegment(sketch, "E3.4.13.1", {"start": v(-46.76, -67.54) * mm, "end": v(-46.76, -72.16) * mm});
            skLineSegment(sketch, "E3.4.13.2", {"start": v(-42.14, -67.54) * mm, "end": v(-42.14, -72.16) * mm});
            skLineSegment(sketch, "E3.4.13.3", {"start": v(-46.76, -72.16) * mm, "end": v(-42.14, -72.16) * mm});
            skLineSegment(sketch, "E3.4.14.0", {"start": v(-46.76, -80.24) * mm, "end": v(-42.14, -80.24) * mm});
            skLineSegment(sketch, "E3.4.14.1", {"start": v(-46.76, -80.24) * mm, "end": v(-46.76, -84.86) * mm});
            skLineSegment(sketch, "E3.4.14.2", {"start": v(-42.14, -80.24) * mm, "end": v(-42.14, -84.86) * mm});
            skLineSegment(sketch, "E3.4.14.3", {"start": v(-46.76, -84.86) * mm, "end": v(-42.14, -84.86) * mm});
            skLineSegment(sketch, "E3.4.15.0", {"start": v(-46.76, -92.94) * mm, "end": v(-42.14, -92.94) * mm});
            skLineSegment(sketch, "E3.4.15.1", {"start": v(-46.76, -92.94) * mm, "end": v(-46.76, -97.56) * mm});
            skLineSegment(sketch, "E3.4.15.2", {"start": v(-42.14, -92.94) * mm, "end": v(-42.14, -97.56) * mm});
            skLineSegment(sketch, "E3.4.15.3", {"start": v(-46.76, -97.56) * mm, "end": v(-42.14, -97.56) * mm});
            skLineSegment(sketch, "E3.4.16.0", {"start": v(-46.76, -105.64) * mm, "end": v(-42.14, -105.64) * mm});
            skLineSegment(sketch, "E3.4.16.1", {"start": v(-46.76, -105.64) * mm, "end": v(-46.76, -110.26) * mm});
            skLineSegment(sketch, "E3.4.16.2", {"start": v(-42.14, -105.64) * mm, "end": v(-42.14, -110.26) * mm});
            skLineSegment(sketch, "E3.4.16.3", {"start": v(-46.76, -110.26) * mm, "end": v(-42.14, -110.26) * mm});
            skLineSegment(sketch, "E3.5.0.0", {"start": v(-34.06, 97.56) * mm, "end": v(-29.44, 97.56) * mm});
            skLineSegment(sketch, "E3.5.0.1", {"start": v(-34.06, 97.56) * mm, "end": v(-34.06, 92.94) * mm});
            skLineSegment(sketch, "E3.5.0.2", {"start": v(-29.44, 97.56) * mm, "end": v(-29.44, 92.94) * mm});
            skLineSegment(sketch, "E3.5.0.3", {"start": v(-34.06, 92.94) * mm, "end": v(-29.44, 92.94) * mm});
            skLineSegment(sketch, "E3.5.1.0", {"start": v(-34.06, 84.86) * mm, "end": v(-29.44, 84.86) * mm});
            skLineSegment(sketch, "E3.5.1.1", {"start": v(-34.06, 84.86) * mm, "end": v(-34.06, 80.24) * mm});
            skLineSegment(sketch, "E3.5.1.2", {"start": v(-29.44, 84.86) * mm, "end": v(-29.44, 80.24) * mm});
            skLineSegment(sketch, "E3.5.1.3", {"start": v(-34.06, 80.24) * mm, "end": v(-29.44, 80.24) * mm});
            skLineSegment(sketch, "E3.5.2.0", {"start": v(-34.06, 72.16) * mm, "end": v(-29.44, 72.16) * mm});
            skLineSegment(sketch, "E3.5.2.1", {"start": v(-34.06, 72.16) * mm, "end": v(-34.06, 67.54) * mm});
            skLineSegment(sketch, "E3.5.2.2", {"start": v(-29.44, 72.16) * mm, "end": v(-29.44, 67.54) * mm});
            skLineSegment(sketch, "E3.5.2.3", {"start": v(-34.06, 67.54) * mm, "end": v(-29.44, 67.54) * mm});
            skLineSegment(sketch, "E3.5.3.0", {"start": v(-34.06, 59.46) * mm, "end": v(-29.44, 59.46) * mm});
            skLineSegment(sketch, "E3.5.3.1", {"start": v(-34.06, 59.46) * mm, "end": v(-34.06, 54.84) * mm});
            skLineSegment(sketch, "E3.5.3.2", {"start": v(-29.44, 59.46) * mm, "end": v(-29.44, 54.84) * mm});
            skLineSegment(sketch, "E3.5.3.3", {"start": v(-34.06, 54.84) * mm, "end": v(-29.44, 54.84) * mm});
            skLineSegment(sketch, "E3.5.4.0", {"start": v(-34.06, 46.76) * mm, "end": v(-29.44, 46.76) * mm});
            skLineSegment(sketch, "E3.5.4.1", {"start": v(-34.06, 46.76) * mm, "end": v(-34.06, 42.14) * mm});
            skLineSegment(sketch, "E3.5.4.2", {"start": v(-29.44, 46.76) * mm, "end": v(-29.44, 42.14) * mm});
            skLineSegment(sketch, "E3.5.4.3", {"start": v(-34.06, 42.14) * mm, "end": v(-29.44, 42.14) * mm});
            skLineSegment(sketch, "E3.5.5.0", {"start": v(-34.06, 34.06) * mm, "end": v(-29.44, 34.06) * mm});
            skLineSegment(sketch, "E3.5.5.1", {"start": v(-34.06, 34.06) * mm, "end": v(-34.06, 29.44) * mm});
            skLineSegment(sketch, "E3.5.5.2", {"start": v(-29.44, 34.06) * mm, "end": v(-29.44, 29.44) * mm});
            skLineSegment(sketch, "E3.5.5.3", {"start": v(-34.06, 29.44) * mm, "end": v(-29.44, 29.44) * mm});
            skLineSegment(sketch, "E3.5.6.0", {"start": v(-34.06, 21.36) * mm, "end": v(-29.44, 21.36) * mm});
            skLineSegment(sketch, "E3.5.6.1", {"start": v(-34.06, 21.36) * mm, "end": v(-34.06, 16.74) * mm});
            skLineSegment(sketch, "E3.5.6.2", {"start": v(-29.44, 21.36) * mm, "end": v(-29.44, 16.74) * mm});
            skLineSegment(sketch, "E3.5.6.3", {"start": v(-34.06, 16.74) * mm, "end": v(-29.44, 16.74) * mm});
            skLineSegment(sketch, "E3.5.7.0", {"start": v(-34.06, 8.66) * mm, "end": v(-29.44, 8.66) * mm});
            skLineSegment(sketch, "E3.5.7.1", {"start": v(-34.06, 8.66) * mm, "end": v(-34.06, 4.04) * mm});
            skLineSegment(sketch, "E3.5.7.2", {"start": v(-29.44, 8.66) * mm, "end": v(-29.44, 4.04) * mm});
            skLineSegment(sketch, "E3.5.7.3", {"start": v(-34.06, 4.04) * mm, "end": v(-29.44, 4.04) * mm});
            skLineSegment(sketch, "E3.5.8.0", {"start": v(-34.06, -4.04) * mm, "end": v(-29.44, -4.04) * mm});
            skLineSegment(sketch, "E3.5.8.1", {"start": v(-34.06, -4.04) * mm, "end": v(-34.06, -8.66) * mm});
            skLineSegment(sketch, "E3.5.8.2", {"start": v(-29.44, -4.04) * mm, "end": v(-29.44, -8.66) * mm});
            skLineSegment(sketch, "E3.5.8.3", {"start": v(-34.06, -8.66) * mm, "end": v(-29.44, -8.66) * mm});
            skLineSegment(sketch, "E3.5.9.0", {"start": v(-34.06, -16.74) * mm, "end": v(-29.44, -16.74) * mm});
            skLineSegment(sketch, "E3.5.9.1", {"start": v(-34.06, -16.74) * mm, "end": v(-34.06, -21.36) * mm});
            skLineSegment(sketch, "E3.5.9.2", {"start": v(-29.44, -16.74) * mm, "end": v(-29.44, -21.36) * mm});
            skLineSegment(sketch, "E3.5.9.3", {"start": v(-34.06, -21.36) * mm, "end": v(-29.44, -21.36) * mm});
            skLineSegment(sketch, "E3.5.10.0", {"start": v(-34.06, -29.44) * mm, "end": v(-29.44, -29.44) * mm});
            skLineSegment(sketch, "E3.5.10.1", {"start": v(-34.06, -29.44) * mm, "end": v(-34.06, -34.06) * mm});
            skLineSegment(sketch, "E3.5.10.2", {"start": v(-29.44, -29.44) * mm, "end": v(-29.44, -34.06) * mm});
            skLineSegment(sketch, "E3.5.10.3", {"start": v(-34.06, -34.06) * mm, "end": v(-29.44, -34.06) * mm});
            skLineSegment(sketch, "E3.5.11.0", {"start": v(-34.06, -42.14) * mm, "end": v(-29.44, -42.14) * mm});
            skLineSegment(sketch, "E3.5.11.1", {"start": v(-34.06, -42.14) * mm, "end": v(-34.06, -46.76) * mm});
            skLineSegment(sketch, "E3.5.11.2", {"start": v(-29.44, -42.14) * mm, "end": v(-29.44, -46.76) * mm});
            skLineSegment(sketch, "E3.5.11.3", {"start": v(-34.06, -46.76) * mm, "end": v(-29.44, -46.76) * mm});
            skLineSegment(sketch, "E3.5.12.0", {"start": v(-34.06, -54.84) * mm, "end": v(-29.44, -54.84) * mm});
            skLineSegment(sketch, "E3.5.12.1", {"start": v(-34.06, -54.84) * mm, "end": v(-34.06, -59.46) * mm});
            skLineSegment(sketch, "E3.5.12.2", {"start": v(-29.44, -54.84) * mm, "end": v(-29.44, -59.46) * mm});
            skLineSegment(sketch, "E3.5.12.3", {"start": v(-34.06, -59.46) * mm, "end": v(-29.44, -59.46) * mm});
            skLineSegment(sketch, "E3.5.13.0", {"start": v(-34.06, -67.54) * mm, "end": v(-29.44, -67.54) * mm});
            skLineSegment(sketch, "E3.5.13.1", {"start": v(-34.06, -67.54) * mm, "end": v(-34.06, -72.16) * mm});
            skLineSegment(sketch, "E3.5.13.2", {"start": v(-29.44, -67.54) * mm, "end": v(-29.44, -72.16) * mm});
            skLineSegment(sketch, "E3.5.13.3", {"start": v(-34.06, -72.16) * mm, "end": v(-29.44, -72.16) * mm});
            skLineSegment(sketch, "E3.5.14.0", {"start": v(-34.06, -80.24) * mm, "end": v(-29.44, -80.24) * mm});
            skLineSegment(sketch, "E3.5.14.1", {"start": v(-34.06, -80.24) * mm, "end": v(-34.06, -84.86) * mm});
            skLineSegment(sketch, "E3.5.14.2", {"start": v(-29.44, -80.24) * mm, "end": v(-29.44, -84.86) * mm});
            skLineSegment(sketch, "E3.5.14.3", {"start": v(-34.06, -84.86) * mm, "end": v(-29.44, -84.86) * mm});
            skLineSegment(sketch, "E3.5.15.0", {"start": v(-34.06, -92.94) * mm, "end": v(-29.44, -92.94) * mm});
            skLineSegment(sketch, "E3.5.15.1", {"start": v(-34.06, -92.94) * mm, "end": v(-34.06, -97.56) * mm});
            skLineSegment(sketch, "E3.5.15.2", {"start": v(-29.44, -92.94) * mm, "end": v(-29.44, -97.56) * mm});
            skLineSegment(sketch, "E3.5.15.3", {"start": v(-34.06, -97.56) * mm, "end": v(-29.44, -97.56) * mm});
            skLineSegment(sketch, "E3.5.16.0", {"start": v(-34.06, -105.64) * mm, "end": v(-29.44, -105.64) * mm});
            skLineSegment(sketch, "E3.5.16.1", {"start": v(-34.06, -105.64) * mm, "end": v(-34.06, -110.26) * mm});
            skLineSegment(sketch, "E3.5.16.2", {"start": v(-29.44, -105.64) * mm, "end": v(-29.44, -110.26) * mm});
            skLineSegment(sketch, "E3.5.16.3", {"start": v(-34.06, -110.26) * mm, "end": v(-29.44, -110.26) * mm});
            skLineSegment(sketch, "E3.6.0.0", {"start": v(-21.36, 97.56) * mm, "end": v(-16.74, 97.56) * mm});
            skLineSegment(sketch, "E3.6.0.1", {"start": v(-21.36, 97.56) * mm, "end": v(-21.36, 92.94) * mm});
            skLineSegment(sketch, "E3.6.0.2", {"start": v(-16.74, 97.56) * mm, "end": v(-16.74, 92.94) * mm});
            skLineSegment(sketch, "E3.6.0.3", {"start": v(-21.36, 92.94) * mm, "end": v(-16.74, 92.94) * mm});
            skLineSegment(sketch, "E3.6.1.0", {"start": v(-21.36, 84.86) * mm, "end": v(-16.74, 84.86) * mm});
            skLineSegment(sketch, "E3.6.1.1", {"start": v(-21.36, 84.86) * mm, "end": v(-21.36, 80.24) * mm});
            skLineSegment(sketch, "E3.6.1.2", {"start": v(-16.74, 84.86) * mm, "end": v(-16.74, 80.24) * mm});
            skLineSegment(sketch, "E3.6.1.3", {"start": v(-21.36, 80.24) * mm, "end": v(-16.74, 80.24) * mm});
            skLineSegment(sketch, "E3.6.2.0", {"start": v(-21.36, 72.16) * mm, "end": v(-16.74, 72.16) * mm});
            skLineSegment(sketch, "E3.6.2.1", {"start": v(-21.36, 72.16) * mm, "end": v(-21.36, 67.54) * mm});
            skLineSegment(sketch, "E3.6.2.2", {"start": v(-16.74, 72.16) * mm, "end": v(-16.74, 67.54) * mm});
            skLineSegment(sketch, "E3.6.2.3", {"start": v(-21.36, 67.54) * mm, "end": v(-16.74, 67.54) * mm});
            skLineSegment(sketch, "E3.6.3.0", {"start": v(-21.36, 59.46) * mm, "end": v(-16.74, 59.46) * mm});
            skLineSegment(sketch, "E3.6.3.1", {"start": v(-21.36, 59.46) * mm, "end": v(-21.36, 54.84) * mm});
            skLineSegment(sketch, "E3.6.3.2", {"start": v(-16.74, 59.46) * mm, "end": v(-16.74, 54.84) * mm});
            skLineSegment(sketch, "E3.6.3.3", {"start": v(-21.36, 54.84) * mm, "end": v(-16.74, 54.84) * mm});
            skLineSegment(sketch, "E3.6.4.0", {"start": v(-21.36, 46.76) * mm, "end": v(-16.74, 46.76) * mm});
            skLineSegment(sketch, "E3.6.4.1", {"start": v(-21.36, 46.76) * mm, "end": v(-21.36, 42.14) * mm});
            skLineSegment(sketch, "E3.6.4.2", {"start": v(-16.74, 46.76) * mm, "end": v(-16.74, 42.14) * mm});
            skLineSegment(sketch, "E3.6.4.3", {"start": v(-21.36, 42.14) * mm, "end": v(-16.74, 42.14) * mm});
            skLineSegment(sketch, "E3.6.5.0", {"start": v(-21.36, 34.06) * mm, "end": v(-16.74, 34.06) * mm});
            skLineSegment(sketch, "E3.6.5.1", {"start": v(-21.36, 34.06) * mm, "end": v(-21.36, 29.44) * mm});
            skLineSegment(sketch, "E3.6.5.2", {"start": v(-16.74, 34.06) * mm, "end": v(-16.74, 29.44) * mm});
            skLineSegment(sketch, "E3.6.5.3", {"start": v(-21.36, 29.44) * mm, "end": v(-16.74, 29.44) * mm});
            skLineSegment(sketch, "E3.6.6.0", {"start": v(-21.36, 21.36) * mm, "end": v(-16.74, 21.36) * mm});
            skLineSegment(sketch, "E3.6.6.1", {"start": v(-21.36, 21.36) * mm, "end": v(-21.36, 16.74) * mm});
            skLineSegment(sketch, "E3.6.6.2", {"start": v(-16.74, 21.36) * mm, "end": v(-16.74, 16.74) * mm});
            skLineSegment(sketch, "E3.6.6.3", {"start": v(-21.36, 16.74) * mm, "end": v(-16.74, 16.74) * mm});
            skLineSegment(sketch, "E3.6.7.0", {"start": v(-21.36, 8.66) * mm, "end": v(-16.74, 8.66) * mm});
            skLineSegment(sketch, "E3.6.7.1", {"start": v(-21.36, 8.66) * mm, "end": v(-21.36, 4.04) * mm});
            skLineSegment(sketch, "E3.6.7.2", {"start": v(-16.74, 8.66) * mm, "end": v(-16.74, 4.04) * mm});
            skLineSegment(sketch, "E3.6.7.3", {"start": v(-21.36, 4.04) * mm, "end": v(-16.74, 4.04) * mm});
            skLineSegment(sketch, "E3.6.8.0", {"start": v(-21.36, -4.04) * mm, "end": v(-16.74, -4.04) * mm});
            skLineSegment(sketch, "E3.6.8.1", {"start": v(-21.36, -4.04) * mm, "end": v(-21.36, -8.66) * mm});
            skLineSegment(sketch, "E3.6.8.2", {"start": v(-16.74, -4.04) * mm, "end": v(-16.74, -8.66) * mm});
            skLineSegment(sketch, "E3.6.8.3", {"start": v(-21.36, -8.66) * mm, "end": v(-16.74, -8.66) * mm});
            skLineSegment(sketch, "E3.6.9.0", {"start": v(-21.36, -16.74) * mm, "end": v(-16.74, -16.74) * mm});
            skLineSegment(sketch, "E3.6.9.1", {"start": v(-21.36, -16.74) * mm, "end": v(-21.36, -21.36) * mm});
            skLineSegment(sketch, "E3.6.9.2", {"start": v(-16.74, -16.74) * mm, "end": v(-16.74, -21.36) * mm});
            skLineSegment(sketch, "E3.6.9.3", {"start": v(-21.36, -21.36) * mm, "end": v(-16.74, -21.36) * mm});
            skLineSegment(sketch, "E3.6.10.0", {"start": v(-21.36, -29.44) * mm, "end": v(-16.74, -29.44) * mm});
            skLineSegment(sketch, "E3.6.10.1", {"start": v(-21.36, -29.44) * mm, "end": v(-21.36, -34.06) * mm});
            skLineSegment(sketch, "E3.6.10.2", {"start": v(-16.74, -29.44) * mm, "end": v(-16.74, -34.06) * mm});
            skLineSegment(sketch, "E3.6.10.3", {"start": v(-21.36, -34.06) * mm, "end": v(-16.74, -34.06) * mm});
            skLineSegment(sketch, "E3.6.11.0", {"start": v(-21.36, -42.14) * mm, "end": v(-16.74, -42.14) * mm});
            skLineSegment(sketch, "E3.6.11.1", {"start": v(-21.36, -42.14) * mm, "end": v(-21.36, -46.76) * mm});
            skLineSegment(sketch, "E3.6.11.2", {"start": v(-16.74, -42.14) * mm, "end": v(-16.74, -46.76) * mm});
            skLineSegment(sketch, "E3.6.11.3", {"start": v(-21.36, -46.76) * mm, "end": v(-16.74, -46.76) * mm});
            skLineSegment(sketch, "E3.6.12.0", {"start": v(-21.36, -54.84) * mm, "end": v(-16.74, -54.84) * mm});
            skLineSegment(sketch, "E3.6.12.1", {"start": v(-21.36, -54.84) * mm, "end": v(-21.36, -59.46) * mm});
            skLineSegment(sketch, "E3.6.12.2", {"start": v(-16.74, -54.84) * mm, "end": v(-16.74, -59.46) * mm});
            skLineSegment(sketch, "E3.6.12.3", {"start": v(-21.36, -59.46) * mm, "end": v(-16.74, -59.46) * mm});
            skLineSegment(sketch, "E3.6.13.0", {"start": v(-21.36, -67.54) * mm, "end": v(-16.74, -67.54) * mm});
            skLineSegment(sketch, "E3.6.13.1", {"start": v(-21.36, -67.54) * mm, "end": v(-21.36, -72.16) * mm});
            skLineSegment(sketch, "E3.6.13.2", {"start": v(-16.74, -67.54) * mm, "end": v(-16.74, -72.16) * mm});
            skLineSegment(sketch, "E3.6.13.3", {"start": v(-21.36, -72.16) * mm, "end": v(-16.74, -72.16) * mm});
            skLineSegment(sketch, "E3.6.14.0", {"start": v(-21.36, -80.24) * mm, "end": v(-16.74, -80.24) * mm});
            skLineSegment(sketch, "E3.6.14.1", {"start": v(-21.36, -80.24) * mm, "end": v(-21.36, -84.86) * mm});
            skLineSegment(sketch, "E3.6.14.2", {"start": v(-16.74, -80.24) * mm, "end": v(-16.74, -84.86) * mm});
            skLineSegment(sketch, "E3.6.14.3", {"start": v(-21.36, -84.86) * mm, "end": v(-16.74, -84.86) * mm});
            skLineSegment(sketch, "E3.6.15.0", {"start": v(-21.36, -92.94) * mm, "end": v(-16.74, -92.94) * mm});
            skLineSegment(sketch, "E3.6.15.1", {"start": v(-21.36, -92.94) * mm, "end": v(-21.36, -97.56) * mm});
            skLineSegment(sketch, "E3.6.15.2", {"start": v(-16.74, -92.94) * mm, "end": v(-16.74, -97.56) * mm});
            skLineSegment(sketch, "E3.6.15.3", {"start": v(-21.36, -97.56) * mm, "end": v(-16.74, -97.56) * mm});
            skLineSegment(sketch, "E3.6.16.0", {"start": v(-21.36, -105.64) * mm, "end": v(-16.74, -105.64) * mm});
            skLineSegment(sketch, "E3.6.16.1", {"start": v(-21.36, -105.64) * mm, "end": v(-21.36, -110.26) * mm});
            skLineSegment(sketch, "E3.6.16.2", {"start": v(-16.74, -105.64) * mm, "end": v(-16.74, -110.26) * mm});
            skLineSegment(sketch, "E3.6.16.3", {"start": v(-21.36, -110.26) * mm, "end": v(-16.74, -110.26) * mm});
            skLineSegment(sketch, "E3.7.0.0", {"start": v(-8.66, 97.56) * mm, "end": v(-4.04, 97.56) * mm});
            skLineSegment(sketch, "E3.7.0.1", {"start": v(-8.66, 97.56) * mm, "end": v(-8.66, 92.94) * mm});
            skLineSegment(sketch, "E3.7.0.2", {"start": v(-4.04, 97.56) * mm, "end": v(-4.04, 92.94) * mm});
            skLineSegment(sketch, "E3.7.0.3", {"start": v(-8.66, 92.94) * mm, "end": v(-4.04, 92.94) * mm});
            skLineSegment(sketch, "E3.7.1.0", {"start": v(-8.66, 84.86) * mm, "end": v(-4.04, 84.86) * mm});
            skLineSegment(sketch, "E3.7.1.1", {"start": v(-8.66, 84.86) * mm, "end": v(-8.66, 80.24) * mm});
            skLineSegment(sketch, "E3.7.1.2", {"start": v(-4.04, 84.86) * mm, "end": v(-4.04, 80.24) * mm});
            skLineSegment(sketch, "E3.7.1.3", {"start": v(-8.66, 80.24) * mm, "end": v(-4.04, 80.24) * mm});
            skLineSegment(sketch, "E3.7.2.0", {"start": v(-8.66, 72.16) * mm, "end": v(-4.04, 72.16) * mm});
            skLineSegment(sketch, "E3.7.2.1", {"start": v(-8.66, 72.16) * mm, "end": v(-8.66, 67.54) * mm});
            skLineSegment(sketch, "E3.7.2.2", {"start": v(-4.04, 72.16) * mm, "end": v(-4.04, 67.54) * mm});
            skLineSegment(sketch, "E3.7.2.3", {"start": v(-8.66, 67.54) * mm, "end": v(-4.04, 67.54) * mm});
            skLineSegment(sketch, "E3.7.3.0", {"start": v(-8.66, 59.46) * mm, "end": v(-4.04, 59.46) * mm});
            skLineSegment(sketch, "E3.7.3.1", {"start": v(-8.66, 59.46) * mm, "end": v(-8.66, 54.84) * mm});
            skLineSegment(sketch, "E3.7.3.2", {"start": v(-4.04, 59.46) * mm, "end": v(-4.04, 54.84) * mm});
            skLineSegment(sketch, "E3.7.3.3", {"start": v(-8.66, 54.84) * mm, "end": v(-4.04, 54.84) * mm});
            skLineSegment(sketch, "E3.7.4.0", {"start": v(-8.66, 46.76) * mm, "end": v(-4.04, 46.76) * mm});
            skLineSegment(sketch, "E3.7.4.1", {"start": v(-8.66, 46.76) * mm, "end": v(-8.66, 42.14) * mm});
            skLineSegment(sketch, "E3.7.4.2", {"start": v(-4.04, 46.76) * mm, "end": v(-4.04, 42.14) * mm});
            skLineSegment(sketch, "E3.7.4.3", {"start": v(-8.66, 42.14) * mm, "end": v(-4.04, 42.14) * mm});
            skLineSegment(sketch, "E3.7.5.0", {"start": v(-8.66, 34.06) * mm, "end": v(-4.04, 34.06) * mm});
            skLineSegment(sketch, "E3.7.5.1", {"start": v(-8.66, 34.06) * mm, "end": v(-8.66, 29.44) * mm});
            skLineSegment(sketch, "E3.7.5.2", {"start": v(-4.04, 34.06) * mm, "end": v(-4.04, 29.44) * mm});
            skLineSegment(sketch, "E3.7.5.3", {"start": v(-8.66, 29.44) * mm, "end": v(-4.04, 29.44) * mm});
            skLineSegment(sketch, "E3.7.6.0", {"start": v(-8.66, 21.36) * mm, "end": v(-4.04, 21.36) * mm});
            skLineSegment(sketch, "E3.7.6.1", {"start": v(-8.66, 21.36) * mm, "end": v(-8.66, 16.74) * mm});
            skLineSegment(sketch, "E3.7.6.2", {"start": v(-4.04, 21.36) * mm, "end": v(-4.04, 16.74) * mm});
            skLineSegment(sketch, "E3.7.6.3", {"start": v(-8.66, 16.74) * mm, "end": v(-4.04, 16.74) * mm});
            skLineSegment(sketch, "E3.7.7.0", {"start": v(-8.66, 8.66) * mm, "end": v(-4.04, 8.66) * mm});
            skLineSegment(sketch, "E3.7.7.1", {"start": v(-8.66, 8.66) * mm, "end": v(-8.66, 4.04) * mm});
            skLineSegment(sketch, "E3.7.7.2", {"start": v(-4.04, 8.66) * mm, "end": v(-4.04, 4.04) * mm});
            skLineSegment(sketch, "E3.7.7.3", {"start": v(-8.66, 4.04) * mm, "end": v(-4.04, 4.04) * mm});
            skLineSegment(sketch, "E3.7.8.0", {"start": v(-8.66, -4.04) * mm, "end": v(-4.04, -4.04) * mm});
            skLineSegment(sketch, "E3.7.8.1", {"start": v(-8.66, -4.04) * mm, "end": v(-8.66, -8.66) * mm});
            skLineSegment(sketch, "E3.7.8.2", {"start": v(-4.04, -4.04) * mm, "end": v(-4.04, -8.66) * mm});
            skLineSegment(sketch, "E3.7.8.3", {"start": v(-8.66, -8.66) * mm, "end": v(-4.04, -8.66) * mm});
            skLineSegment(sketch, "E3.7.9.0", {"start": v(-8.66, -16.74) * mm, "end": v(-4.04, -16.74) * mm});
            skLineSegment(sketch, "E3.7.9.1", {"start": v(-8.66, -16.74) * mm, "end": v(-8.66, -21.36) * mm});
            skLineSegment(sketch, "E3.7.9.2", {"start": v(-4.04, -16.74) * mm, "end": v(-4.04, -21.36) * mm});
            skLineSegment(sketch, "E3.7.9.3", {"start": v(-8.66, -21.36) * mm, "end": v(-4.04, -21.36) * mm});
            skLineSegment(sketch, "E3.7.10.0", {"start": v(-8.66, -29.44) * mm, "end": v(-4.04, -29.44) * mm});
            skLineSegment(sketch, "E3.7.10.1", {"start": v(-8.66, -29.44) * mm, "end": v(-8.66, -34.06) * mm});
            skLineSegment(sketch, "E3.7.10.2", {"start": v(-4.04, -29.44) * mm, "end": v(-4.04, -34.06) * mm});
            skLineSegment(sketch, "E3.7.10.3", {"start": v(-8.66, -34.06) * mm, "end": v(-4.04, -34.06) * mm});
            skLineSegment(sketch, "E3.7.11.0", {"start": v(-8.66, -42.14) * mm, "end": v(-4.04, -42.14) * mm});
            skLineSegment(sketch, "E3.7.11.1", {"start": v(-8.66, -42.14) * mm, "end": v(-8.66, -46.76) * mm});
            skLineSegment(sketch, "E3.7.11.2", {"start": v(-4.04, -42.14) * mm, "end": v(-4.04, -46.76) * mm});
            skLineSegment(sketch, "E3.7.11.3", {"start": v(-8.66, -46.76) * mm, "end": v(-4.04, -46.76) * mm});
            skLineSegment(sketch, "E3.7.12.0", {"start": v(-8.66, -54.84) * mm, "end": v(-4.04, -54.84) * mm});
            skLineSegment(sketch, "E3.7.12.1", {"start": v(-8.66, -54.84) * mm, "end": v(-8.66, -59.46) * mm});
            skLineSegment(sketch, "E3.7.12.2", {"start": v(-4.04, -54.84) * mm, "end": v(-4.04, -59.46) * mm});
            skLineSegment(sketch, "E3.7.12.3", {"start": v(-8.66, -59.46) * mm, "end": v(-4.04, -59.46) * mm});
            skLineSegment(sketch, "E3.7.13.0", {"start": v(-8.66, -67.54) * mm, "end": v(-4.04, -67.54) * mm});
            skLineSegment(sketch, "E3.7.13.1", {"start": v(-8.66, -67.54) * mm, "end": v(-8.66, -72.16) * mm});
            skLineSegment(sketch, "E3.7.13.2", {"start": v(-4.04, -67.54) * mm, "end": v(-4.04, -72.16) * mm});
            skLineSegment(sketch, "E3.7.13.3", {"start": v(-8.66, -72.16) * mm, "end": v(-4.04, -72.16) * mm});
            skLineSegment(sketch, "E3.7.14.0", {"start": v(-8.66, -80.24) * mm, "end": v(-4.04, -80.24) * mm});
            skLineSegment(sketch, "E3.7.14.1", {"start": v(-8.66, -80.24) * mm, "end": v(-8.66, -84.86) * mm});
            skLineSegment(sketch, "E3.7.14.2", {"start": v(-4.04, -80.24) * mm, "end": v(-4.04, -84.86) * mm});
            skLineSegment(sketch, "E3.7.14.3", {"start": v(-8.66, -84.86) * mm, "end": v(-4.04, -84.86) * mm});
            skLineSegment(sketch, "E3.7.15.0", {"start": v(-8.66, -92.94) * mm, "end": v(-4.04, -92.94) * mm});
            skLineSegment(sketch, "E3.7.15.1", {"start": v(-8.66, -92.94) * mm, "end": v(-8.66, -97.56) * mm});
            skLineSegment(sketch, "E3.7.15.2", {"start": v(-4.04, -92.94) * mm, "end": v(-4.04, -97.56) * mm});
            skLineSegment(sketch, "E3.7.15.3", {"start": v(-8.66, -97.56) * mm, "end": v(-4.04, -97.56) * mm});
            skLineSegment(sketch, "E3.7.16.0", {"start": v(-8.66, -105.64) * mm, "end": v(-4.04, -105.64) * mm});
            skLineSegment(sketch, "E3.7.16.1", {"start": v(-8.66, -105.64) * mm, "end": v(-8.66, -110.26) * mm});
            skLineSegment(sketch, "E3.7.16.2", {"start": v(-4.04, -105.64) * mm, "end": v(-4.04, -110.26) * mm});
            skLineSegment(sketch, "E3.7.16.3", {"start": v(-8.66, -110.26) * mm, "end": v(-4.04, -110.26) * mm});
            skLineSegment(sketch, "E3.8.0.0", {"start": v(4.04, 97.56) * mm, "end": v(8.66, 97.56) * mm});
            skLineSegment(sketch, "E3.8.0.1", {"start": v(4.04, 97.56) * mm, "end": v(4.04, 92.94) * mm});
            skLineSegment(sketch, "E3.8.0.2", {"start": v(8.66, 97.56) * mm, "end": v(8.66, 92.94) * mm});
            skLineSegment(sketch, "E3.8.0.3", {"start": v(4.04, 92.94) * mm, "end": v(8.66, 92.94) * mm});
            skLineSegment(sketch, "E3.8.1.0", {"start": v(4.04, 84.86) * mm, "end": v(8.66, 84.86) * mm});
            skLineSegment(sketch, "E3.8.1.1", {"start": v(4.04, 84.86) * mm, "end": v(4.04, 80.24) * mm});
            skLineSegment(sketch, "E3.8.1.2", {"start": v(8.66, 84.86) * mm, "end": v(8.66, 80.24) * mm});
            skLineSegment(sketch, "E3.8.1.3", {"start": v(4.04, 80.24) * mm, "end": v(8.66, 80.24) * mm});
            skLineSegment(sketch, "E3.8.2.0", {"start": v(4.04, 72.16) * mm, "end": v(8.66, 72.16) * mm});
            skLineSegment(sketch, "E3.8.2.1", {"start": v(4.04, 72.16) * mm, "end": v(4.04, 67.54) * mm});
            skLineSegment(sketch, "E3.8.2.2", {"start": v(8.66, 72.16) * mm, "end": v(8.66, 67.54) * mm});
            skLineSegment(sketch, "E3.8.2.3", {"start": v(4.04, 67.54) * mm, "end": v(8.66, 67.54) * mm});
            skLineSegment(sketch, "E3.8.3.0", {"start": v(4.04, 59.46) * mm, "end": v(8.66, 59.46) * mm});
            skLineSegment(sketch, "E3.8.3.1", {"start": v(4.04, 59.46) * mm, "end": v(4.04, 54.84) * mm});
            skLineSegment(sketch, "E3.8.3.2", {"start": v(8.66, 59.46) * mm, "end": v(8.66, 54.84) * mm});
            skLineSegment(sketch, "E3.8.3.3", {"start": v(4.04, 54.84) * mm, "end": v(8.66, 54.84) * mm});
            skLineSegment(sketch, "E3.8.4.0", {"start": v(4.04, 46.76) * mm, "end": v(8.66, 46.76) * mm});
            skLineSegment(sketch, "E3.8.4.1", {"start": v(4.04, 46.76) * mm, "end": v(4.04, 42.14) * mm});
            skLineSegment(sketch, "E3.8.4.2", {"start": v(8.66, 46.76) * mm, "end": v(8.66, 42.14) * mm});
            skLineSegment(sketch, "E3.8.4.3", {"start": v(4.04, 42.14) * mm, "end": v(8.66, 42.14) * mm});
            skLineSegment(sketch, "E3.8.5.0", {"start": v(4.04, 34.06) * mm, "end": v(8.66, 34.06) * mm});
            skLineSegment(sketch, "E3.8.5.1", {"start": v(4.04, 34.06) * mm, "end": v(4.04, 29.44) * mm});
            skLineSegment(sketch, "E3.8.5.2", {"start": v(8.66, 34.06) * mm, "end": v(8.66, 29.44) * mm});
            skLineSegment(sketch, "E3.8.5.3", {"start": v(4.04, 29.44) * mm, "end": v(8.66, 29.44) * mm});
            skLineSegment(sketch, "E3.8.6.0", {"start": v(4.04, 21.36) * mm, "end": v(8.66, 21.36) * mm});
            skLineSegment(sketch, "E3.8.6.1", {"start": v(4.04, 21.36) * mm, "end": v(4.04, 16.74) * mm});
            skLineSegment(sketch, "E3.8.6.2", {"start": v(8.66, 21.36) * mm, "end": v(8.66, 16.74) * mm});
            skLineSegment(sketch, "E3.8.6.3", {"start": v(4.04, 16.74) * mm, "end": v(8.66, 16.74) * mm});
            skLineSegment(sketch, "E3.8.7.0", {"start": v(4.04, 8.66) * mm, "end": v(8.66, 8.66) * mm});
            skLineSegment(sketch, "E3.8.7.1", {"start": v(4.04, 8.66) * mm, "end": v(4.04, 4.04) * mm});
            skLineSegment(sketch, "E3.8.7.2", {"start": v(8.66, 8.66) * mm, "end": v(8.66, 4.04) * mm});
            skLineSegment(sketch, "E3.8.7.3", {"start": v(4.04, 4.04) * mm, "end": v(8.66, 4.04) * mm});
            skLineSegment(sketch, "E3.8.8.0", {"start": v(4.04, -4.04) * mm, "end": v(8.66, -4.04) * mm});
            skLineSegment(sketch, "E3.8.8.1", {"start": v(4.04, -4.04) * mm, "end": v(4.04, -8.66) * mm});
            skLineSegment(sketch, "E3.8.8.2", {"start": v(8.66, -4.04) * mm, "end": v(8.66, -8.66) * mm});
            skLineSegment(sketch, "E3.8.8.3", {"start": v(4.04, -8.66) * mm, "end": v(8.66, -8.66) * mm});
            skLineSegment(sketch, "E3.8.9.0", {"start": v(4.04, -16.74) * mm, "end": v(8.66, -16.74) * mm});
            skLineSegment(sketch, "E3.8.9.1", {"start": v(4.04, -16.74) * mm, "end": v(4.04, -21.36) * mm});
            skLineSegment(sketch, "E3.8.9.2", {"start": v(8.66, -16.74) * mm, "end": v(8.66, -21.36) * mm});
            skLineSegment(sketch, "E3.8.9.3", {"start": v(4.04, -21.36) * mm, "end": v(8.66, -21.36) * mm});
            skLineSegment(sketch, "E3.8.10.0", {"start": v(4.04, -29.44) * mm, "end": v(8.66, -29.44) * mm});
            skLineSegment(sketch, "E3.8.10.1", {"start": v(4.04, -29.44) * mm, "end": v(4.04, -34.06) * mm});
            skLineSegment(sketch, "E3.8.10.2", {"start": v(8.66, -29.44) * mm, "end": v(8.66, -34.06) * mm});
            skLineSegment(sketch, "E3.8.10.3", {"start": v(4.04, -34.06) * mm, "end": v(8.66, -34.06) * mm});
            skLineSegment(sketch, "E3.8.11.0", {"start": v(4.04, -42.14) * mm, "end": v(8.66, -42.14) * mm});
            skLineSegment(sketch, "E3.8.11.1", {"start": v(4.04, -42.14) * mm, "end": v(4.04, -46.76) * mm});
            skLineSegment(sketch, "E3.8.11.2", {"start": v(8.66, -42.14) * mm, "end": v(8.66, -46.76) * mm});
            skLineSegment(sketch, "E3.8.11.3", {"start": v(4.04, -46.76) * mm, "end": v(8.66, -46.76) * mm});
            skLineSegment(sketch, "E3.8.12.0", {"start": v(4.04, -54.84) * mm, "end": v(8.66, -54.84) * mm});
            skLineSegment(sketch, "E3.8.12.1", {"start": v(4.04, -54.84) * mm, "end": v(4.04, -59.46) * mm});
            skLineSegment(sketch, "E3.8.12.2", {"start": v(8.66, -54.84) * mm, "end": v(8.66, -59.46) * mm});
            skLineSegment(sketch, "E3.8.12.3", {"start": v(4.04, -59.46) * mm, "end": v(8.66, -59.46) * mm});
            skLineSegment(sketch, "E3.8.13.0", {"start": v(4.04, -67.54) * mm, "end": v(8.66, -67.54) * mm});
            skLineSegment(sketch, "E3.8.13.1", {"start": v(4.04, -67.54) * mm, "end": v(4.04, -72.16) * mm});
            skLineSegment(sketch, "E3.8.13.2", {"start": v(8.66, -67.54) * mm, "end": v(8.66, -72.16) * mm});
            skLineSegment(sketch, "E3.8.13.3", {"start": v(4.04, -72.16) * mm, "end": v(8.66, -72.16) * mm});
            skLineSegment(sketch, "E3.8.14.0", {"start": v(4.04, -80.24) * mm, "end": v(8.66, -80.24) * mm});
            skLineSegment(sketch, "E3.8.14.1", {"start": v(4.04, -80.24) * mm, "end": v(4.04, -84.86) * mm});
            skLineSegment(sketch, "E3.8.14.2", {"start": v(8.66, -80.24) * mm, "end": v(8.66, -84.86) * mm});
            skLineSegment(sketch, "E3.8.14.3", {"start": v(4.04, -84.86) * mm, "end": v(8.66, -84.86) * mm});
            skLineSegment(sketch, "E3.8.15.0", {"start": v(4.04, -92.94) * mm, "end": v(8.66, -92.94) * mm});
            skLineSegment(sketch, "E3.8.15.1", {"start": v(4.04, -92.94) * mm, "end": v(4.04, -97.56) * mm});
            skLineSegment(sketch, "E3.8.15.2", {"start": v(8.66, -92.94) * mm, "end": v(8.66, -97.56) * mm});
            skLineSegment(sketch, "E3.8.15.3", {"start": v(4.04, -97.56) * mm, "end": v(8.66, -97.56) * mm});
            skLineSegment(sketch, "E3.8.16.0", {"start": v(4.04, -105.64) * mm, "end": v(8.66, -105.64) * mm});
            skLineSegment(sketch, "E3.8.16.1", {"start": v(4.04, -105.64) * mm, "end": v(4.04, -110.26) * mm});
            skLineSegment(sketch, "E3.8.16.2", {"start": v(8.66, -105.64) * mm, "end": v(8.66, -110.26) * mm});
            skLineSegment(sketch, "E3.8.16.3", {"start": v(4.04, -110.26) * mm, "end": v(8.66, -110.26) * mm});
            skLineSegment(sketch, "E3.9.0.0", {"start": v(16.74, 97.56) * mm, "end": v(21.36, 97.56) * mm});
            skLineSegment(sketch, "E3.9.0.1", {"start": v(16.74, 97.56) * mm, "end": v(16.74, 92.94) * mm});
            skLineSegment(sketch, "E3.9.0.2", {"start": v(21.36, 97.56) * mm, "end": v(21.36, 92.94) * mm});
            skLineSegment(sketch, "E3.9.0.3", {"start": v(16.74, 92.94) * mm, "end": v(21.36, 92.94) * mm});
            skLineSegment(sketch, "E3.9.1.0", {"start": v(16.74, 84.86) * mm, "end": v(21.36, 84.86) * mm});
            skLineSegment(sketch, "E3.9.1.1", {"start": v(16.74, 84.86) * mm, "end": v(16.74, 80.24) * mm});
            skLineSegment(sketch, "E3.9.1.2", {"start": v(21.36, 84.86) * mm, "end": v(21.36, 80.24) * mm});
            skLineSegment(sketch, "E3.9.1.3", {"start": v(16.74, 80.24) * mm, "end": v(21.36, 80.24) * mm});
            skLineSegment(sketch, "E3.9.2.0", {"start": v(16.74, 72.16) * mm, "end": v(21.36, 72.16) * mm});
            skLineSegment(sketch, "E3.9.2.1", {"start": v(16.74, 72.16) * mm, "end": v(16.74, 67.54) * mm});
            skLineSegment(sketch, "E3.9.2.2", {"start": v(21.36, 72.16) * mm, "end": v(21.36, 67.54) * mm});
            skLineSegment(sketch, "E3.9.2.3", {"start": v(16.74, 67.54) * mm, "end": v(21.36, 67.54) * mm});
            skLineSegment(sketch, "E3.9.3.0", {"start": v(16.74, 59.46) * mm, "end": v(21.36, 59.46) * mm});
            skLineSegment(sketch, "E3.9.3.1", {"start": v(16.74, 59.46) * mm, "end": v(16.74, 54.84) * mm});
            skLineSegment(sketch, "E3.9.3.2", {"start": v(21.36, 59.46) * mm, "end": v(21.36, 54.84) * mm});
            skLineSegment(sketch, "E3.9.3.3", {"start": v(16.74, 54.84) * mm, "end": v(21.36, 54.84) * mm});
            skLineSegment(sketch, "E3.9.4.0", {"start": v(16.74, 46.76) * mm, "end": v(21.36, 46.76) * mm});
            skLineSegment(sketch, "E3.9.4.1", {"start": v(16.74, 46.76) * mm, "end": v(16.74, 42.14) * mm});
            skLineSegment(sketch, "E3.9.4.2", {"start": v(21.36, 46.76) * mm, "end": v(21.36, 42.14) * mm});
            skLineSegment(sketch, "E3.9.4.3", {"start": v(16.74, 42.14) * mm, "end": v(21.36, 42.14) * mm});
            skLineSegment(sketch, "E3.9.5.0", {"start": v(16.74, 34.06) * mm, "end": v(21.36, 34.06) * mm});
            skLineSegment(sketch, "E3.9.5.1", {"start": v(16.74, 34.06) * mm, "end": v(16.74, 29.44) * mm});
            skLineSegment(sketch, "E3.9.5.2", {"start": v(21.36, 34.06) * mm, "end": v(21.36, 29.44) * mm});
            skLineSegment(sketch, "E3.9.5.3", {"start": v(16.74, 29.44) * mm, "end": v(21.36, 29.44) * mm});
            skLineSegment(sketch, "E3.9.6.0", {"start": v(16.74, 21.36) * mm, "end": v(21.36, 21.36) * mm});
            skLineSegment(sketch, "E3.9.6.1", {"start": v(16.74, 21.36) * mm, "end": v(16.74, 16.74) * mm});
            skLineSegment(sketch, "E3.9.6.2", {"start": v(21.36, 21.36) * mm, "end": v(21.36, 16.74) * mm});
            skLineSegment(sketch, "E3.9.6.3", {"start": v(16.74, 16.74) * mm, "end": v(21.36, 16.74) * mm});
            skLineSegment(sketch, "E3.9.7.0", {"start": v(16.74, 8.66) * mm, "end": v(21.36, 8.66) * mm});
            skLineSegment(sketch, "E3.9.7.1", {"start": v(16.74, 8.66) * mm, "end": v(16.74, 4.04) * mm});
            skLineSegment(sketch, "E3.9.7.2", {"start": v(21.36, 8.66) * mm, "end": v(21.36, 4.04) * mm});
            skLineSegment(sketch, "E3.9.7.3", {"start": v(16.74, 4.04) * mm, "end": v(21.36, 4.04) * mm});
            skLineSegment(sketch, "E3.9.8.0", {"start": v(16.74, -4.04) * mm, "end": v(21.36, -4.04) * mm});
            skLineSegment(sketch, "E3.9.8.1", {"start": v(16.74, -4.04) * mm, "end": v(16.74, -8.66) * mm});
            skLineSegment(sketch, "E3.9.8.2", {"start": v(21.36, -4.04) * mm, "end": v(21.36, -8.66) * mm});
            skLineSegment(sketch, "E3.9.8.3", {"start": v(16.74, -8.66) * mm, "end": v(21.36, -8.66) * mm});
            skLineSegment(sketch, "E3.9.9.0", {"start": v(16.74, -16.74) * mm, "end": v(21.36, -16.74) * mm});
            skLineSegment(sketch, "E3.9.9.1", {"start": v(16.74, -16.74) * mm, "end": v(16.74, -21.36) * mm});
            skLineSegment(sketch, "E3.9.9.2", {"start": v(21.36, -16.74) * mm, "end": v(21.36, -21.36) * mm});
            skLineSegment(sketch, "E3.9.9.3", {"start": v(16.74, -21.36) * mm, "end": v(21.36, -21.36) * mm});
            skLineSegment(sketch, "E3.9.10.0", {"start": v(16.74, -29.44) * mm, "end": v(21.36, -29.44) * mm});
            skLineSegment(sketch, "E3.9.10.1", {"start": v(16.74, -29.44) * mm, "end": v(16.74, -34.06) * mm});
            skLineSegment(sketch, "E3.9.10.2", {"start": v(21.36, -29.44) * mm, "end": v(21.36, -34.06) * mm});
            skLineSegment(sketch, "E3.9.10.3", {"start": v(16.74, -34.06) * mm, "end": v(21.36, -34.06) * mm});
            skLineSegment(sketch, "E3.9.11.0", {"start": v(16.74, -42.14) * mm, "end": v(21.36, -42.14) * mm});
            skLineSegment(sketch, "E3.9.11.1", {"start": v(16.74, -42.14) * mm, "end": v(16.74, -46.76) * mm});
            skLineSegment(sketch, "E3.9.11.2", {"start": v(21.36, -42.14) * mm, "end": v(21.36, -46.76) * mm});
            skLineSegment(sketch, "E3.9.11.3", {"start": v(16.74, -46.76) * mm, "end": v(21.36, -46.76) * mm});
            skLineSegment(sketch, "E3.9.12.0", {"start": v(16.74, -54.84) * mm, "end": v(21.36, -54.84) * mm});
            skLineSegment(sketch, "E3.9.12.1", {"start": v(16.74, -54.84) * mm, "end": v(16.74, -59.46) * mm});
            skLineSegment(sketch, "E3.9.12.2", {"start": v(21.36, -54.84) * mm, "end": v(21.36, -59.46) * mm});
            skLineSegment(sketch, "E3.9.12.3", {"start": v(16.74, -59.46) * mm, "end": v(21.36, -59.46) * mm});
            skLineSegment(sketch, "E3.9.13.0", {"start": v(16.74, -67.54) * mm, "end": v(21.36, -67.54) * mm});
            skLineSegment(sketch, "E3.9.13.1", {"start": v(16.74, -67.54) * mm, "end": v(16.74, -72.16) * mm});
            skLineSegment(sketch, "E3.9.13.2", {"start": v(21.36, -67.54) * mm, "end": v(21.36, -72.16) * mm});
            skLineSegment(sketch, "E3.9.13.3", {"start": v(16.74, -72.16) * mm, "end": v(21.36, -72.16) * mm});
            skLineSegment(sketch, "E3.9.14.0", {"start": v(16.74, -80.24) * mm, "end": v(21.36, -80.24) * mm});
            skLineSegment(sketch, "E3.9.14.1", {"start": v(16.74, -80.24) * mm, "end": v(16.74, -84.86) * mm});
            skLineSegment(sketch, "E3.9.14.2", {"start": v(21.36, -80.24) * mm, "end": v(21.36, -84.86) * mm});
            skLineSegment(sketch, "E3.9.14.3", {"start": v(16.74, -84.86) * mm, "end": v(21.36, -84.86) * mm});
            skLineSegment(sketch, "E3.9.15.0", {"start": v(16.74, -92.94) * mm, "end": v(21.36, -92.94) * mm});
            skLineSegment(sketch, "E3.9.15.1", {"start": v(16.74, -92.94) * mm, "end": v(16.74, -97.56) * mm});
            skLineSegment(sketch, "E3.9.15.2", {"start": v(21.36, -92.94) * mm, "end": v(21.36, -97.56) * mm});
            skLineSegment(sketch, "E3.9.15.3", {"start": v(16.74, -97.56) * mm, "end": v(21.36, -97.56) * mm});
            skLineSegment(sketch, "E3.9.16.0", {"start": v(16.74, -105.64) * mm, "end": v(21.36, -105.64) * mm});
            skLineSegment(sketch, "E3.9.16.1", {"start": v(16.74, -105.64) * mm, "end": v(16.74, -110.26) * mm});
            skLineSegment(sketch, "E3.9.16.2", {"start": v(21.36, -105.64) * mm, "end": v(21.36, -110.26) * mm});
            skLineSegment(sketch, "E3.9.16.3", {"start": v(16.74, -110.26) * mm, "end": v(21.36, -110.26) * mm});
            skLineSegment(sketch, "E3.10.0.0", {"start": v(29.44, 97.56) * mm, "end": v(34.06, 97.56) * mm});
            skLineSegment(sketch, "E3.10.0.1", {"start": v(29.44, 97.56) * mm, "end": v(29.44, 92.94) * mm});
            skLineSegment(sketch, "E3.10.0.2", {"start": v(34.06, 97.56) * mm, "end": v(34.06, 92.94) * mm});
            skLineSegment(sketch, "E3.10.0.3", {"start": v(29.44, 92.94) * mm, "end": v(34.06, 92.94) * mm});
            skLineSegment(sketch, "E3.10.1.0", {"start": v(29.44, 84.86) * mm, "end": v(34.06, 84.86) * mm});
            skLineSegment(sketch, "E3.10.1.1", {"start": v(29.44, 84.86) * mm, "end": v(29.44, 80.24) * mm});
            skLineSegment(sketch, "E3.10.1.2", {"start": v(34.06, 84.86) * mm, "end": v(34.06, 80.24) * mm});
            skLineSegment(sketch, "E3.10.1.3", {"start": v(29.44, 80.24) * mm, "end": v(34.06, 80.24) * mm});
            skLineSegment(sketch, "E3.10.2.0", {"start": v(29.44, 72.16) * mm, "end": v(34.06, 72.16) * mm});
            skLineSegment(sketch, "E3.10.2.1", {"start": v(29.44, 72.16) * mm, "end": v(29.44, 67.54) * mm});
            skLineSegment(sketch, "E3.10.2.2", {"start": v(34.06, 72.16) * mm, "end": v(34.06, 67.54) * mm});
            skLineSegment(sketch, "E3.10.2.3", {"start": v(29.44, 67.54) * mm, "end": v(34.06, 67.54) * mm});
            skLineSegment(sketch, "E3.10.3.0", {"start": v(29.44, 59.46) * mm, "end": v(34.06, 59.46) * mm});
            skLineSegment(sketch, "E3.10.3.1", {"start": v(29.44, 59.46) * mm, "end": v(29.44, 54.84) * mm});
            skLineSegment(sketch, "E3.10.3.2", {"start": v(34.06, 59.46) * mm, "end": v(34.06, 54.84) * mm});
            skLineSegment(sketch, "E3.10.3.3", {"start": v(29.44, 54.84) * mm, "end": v(34.06, 54.84) * mm});
            skLineSegment(sketch, "E3.10.4.0", {"start": v(29.44, 46.76) * mm, "end": v(34.06, 46.76) * mm});
            skLineSegment(sketch, "E3.10.4.1", {"start": v(29.44, 46.76) * mm, "end": v(29.44, 42.14) * mm});
            skLineSegment(sketch, "E3.10.4.2", {"start": v(34.06, 46.76) * mm, "end": v(34.06, 42.14) * mm});
            skLineSegment(sketch, "E3.10.4.3", {"start": v(29.44, 42.14) * mm, "end": v(34.06, 42.14) * mm});
            skLineSegment(sketch, "E3.10.5.0", {"start": v(29.44, 34.06) * mm, "end": v(34.06, 34.06) * mm});
            skLineSegment(sketch, "E3.10.5.1", {"start": v(29.44, 34.06) * mm, "end": v(29.44, 29.44) * mm});
            skLineSegment(sketch, "E3.10.5.2", {"start": v(34.06, 34.06) * mm, "end": v(34.06, 29.44) * mm});
            skLineSegment(sketch, "E3.10.5.3", {"start": v(29.44, 29.44) * mm, "end": v(34.06, 29.44) * mm});
            skLineSegment(sketch, "E3.10.6.0", {"start": v(29.44, 21.36) * mm, "end": v(34.06, 21.36) * mm});
            skLineSegment(sketch, "E3.10.6.1", {"start": v(29.44, 21.36) * mm, "end": v(29.44, 16.74) * mm});
            skLineSegment(sketch, "E3.10.6.2", {"start": v(34.06, 21.36) * mm, "end": v(34.06, 16.74) * mm});
            skLineSegment(sketch, "E3.10.6.3", {"start": v(29.44, 16.74) * mm, "end": v(34.06, 16.74) * mm});
            skLineSegment(sketch, "E3.10.7.0", {"start": v(29.44, 8.66) * mm, "end": v(34.06, 8.66) * mm});
            skLineSegment(sketch, "E3.10.7.1", {"start": v(29.44, 8.66) * mm, "end": v(29.44, 4.04) * mm});
            skLineSegment(sketch, "E3.10.7.2", {"start": v(34.06, 8.66) * mm, "end": v(34.06, 4.04) * mm});
            skLineSegment(sketch, "E3.10.7.3", {"start": v(29.44, 4.04) * mm, "end": v(34.06, 4.04) * mm});
            skLineSegment(sketch, "E3.10.8.0", {"start": v(29.44, -4.04) * mm, "end": v(34.06, -4.04) * mm});
            skLineSegment(sketch, "E3.10.8.1", {"start": v(29.44, -4.04) * mm, "end": v(29.44, -8.66) * mm});
            skLineSegment(sketch, "E3.10.8.2", {"start": v(34.06, -4.04) * mm, "end": v(34.06, -8.66) * mm});
            skLineSegment(sketch, "E3.10.8.3", {"start": v(29.44, -8.66) * mm, "end": v(34.06, -8.66) * mm});
            skLineSegment(sketch, "E3.10.9.0", {"start": v(29.44, -16.74) * mm, "end": v(34.06, -16.74) * mm});
            skLineSegment(sketch, "E3.10.9.1", {"start": v(29.44, -16.74) * mm, "end": v(29.44, -21.36) * mm});
            skLineSegment(sketch, "E3.10.9.2", {"start": v(34.06, -16.74) * mm, "end": v(34.06, -21.36) * mm});
            skLineSegment(sketch, "E3.10.9.3", {"start": v(29.44, -21.36) * mm, "end": v(34.06, -21.36) * mm});
            skLineSegment(sketch, "E3.10.10.0", {"start": v(29.44, -29.44) * mm, "end": v(34.06, -29.44) * mm});
            skLineSegment(sketch, "E3.10.10.1", {"start": v(29.44, -29.44) * mm, "end": v(29.44, -34.06) * mm});
            skLineSegment(sketch, "E3.10.10.2", {"start": v(34.06, -29.44) * mm, "end": v(34.06, -34.06) * mm});
            skLineSegment(sketch, "E3.10.10.3", {"start": v(29.44, -34.06) * mm, "end": v(34.06, -34.06) * mm});
            skLineSegment(sketch, "E3.10.11.0", {"start": v(29.44, -42.14) * mm, "end": v(34.06, -42.14) * mm});
            skLineSegment(sketch, "E3.10.11.1", {"start": v(29.44, -42.14) * mm, "end": v(29.44, -46.76) * mm});
            skLineSegment(sketch, "E3.10.11.2", {"start": v(34.06, -42.14) * mm, "end": v(34.06, -46.76) * mm});
            skLineSegment(sketch, "E3.10.11.3", {"start": v(29.44, -46.76) * mm, "end": v(34.06, -46.76) * mm});
            skLineSegment(sketch, "E3.10.12.0", {"start": v(29.44, -54.84) * mm, "end": v(34.06, -54.84) * mm});
            skLineSegment(sketch, "E3.10.12.1", {"start": v(29.44, -54.84) * mm, "end": v(29.44, -59.46) * mm});
            skLineSegment(sketch, "E3.10.12.2", {"start": v(34.06, -54.84) * mm, "end": v(34.06, -59.46) * mm});
            skLineSegment(sketch, "E3.10.12.3", {"start": v(29.44, -59.46) * mm, "end": v(34.06, -59.46) * mm});
            skLineSegment(sketch, "E3.10.13.0", {"start": v(29.44, -67.54) * mm, "end": v(34.06, -67.54) * mm});
            skLineSegment(sketch, "E3.10.13.1", {"start": v(29.44, -67.54) * mm, "end": v(29.44, -72.16) * mm});
            skLineSegment(sketch, "E3.10.13.2", {"start": v(34.06, -67.54) * mm, "end": v(34.06, -72.16) * mm});
            skLineSegment(sketch, "E3.10.13.3", {"start": v(29.44, -72.16) * mm, "end": v(34.06, -72.16) * mm});
            skLineSegment(sketch, "E3.10.14.0", {"start": v(29.44, -80.24) * mm, "end": v(34.06, -80.24) * mm});
            skLineSegment(sketch, "E3.10.14.1", {"start": v(29.44, -80.24) * mm, "end": v(29.44, -84.86) * mm});
            skLineSegment(sketch, "E3.10.14.2", {"start": v(34.06, -80.24) * mm, "end": v(34.06, -84.86) * mm});
            skLineSegment(sketch, "E3.10.14.3", {"start": v(29.44, -84.86) * mm, "end": v(34.06, -84.86) * mm});
            skLineSegment(sketch, "E3.10.15.0", {"start": v(29.44, -92.94) * mm, "end": v(34.06, -92.94) * mm});
            skLineSegment(sketch, "E3.10.15.1", {"start": v(29.44, -92.94) * mm, "end": v(29.44, -97.56) * mm});
            skLineSegment(sketch, "E3.10.15.2", {"start": v(34.06, -92.94) * mm, "end": v(34.06, -97.56) * mm});
            skLineSegment(sketch, "E3.10.15.3", {"start": v(29.44, -97.56) * mm, "end": v(34.06, -97.56) * mm});
            skLineSegment(sketch, "E3.10.16.0", {"start": v(29.44, -105.64) * mm, "end": v(34.06, -105.64) * mm});
            skLineSegment(sketch, "E3.10.16.1", {"start": v(29.44, -105.64) * mm, "end": v(29.44, -110.26) * mm});
            skLineSegment(sketch, "E3.10.16.2", {"start": v(34.06, -105.64) * mm, "end": v(34.06, -110.26) * mm});
            skLineSegment(sketch, "E3.10.16.3", {"start": v(29.44, -110.26) * mm, "end": v(34.06, -110.26) * mm});
            skLineSegment(sketch, "E3.11.0.0", {"start": v(42.14, 97.56) * mm, "end": v(46.76, 97.56) * mm});
            skLineSegment(sketch, "E3.11.0.1", {"start": v(42.14, 97.56) * mm, "end": v(42.14, 92.94) * mm});
            skLineSegment(sketch, "E3.11.0.2", {"start": v(46.76, 97.56) * mm, "end": v(46.76, 92.94) * mm});
            skLineSegment(sketch, "E3.11.0.3", {"start": v(42.14, 92.94) * mm, "end": v(46.76, 92.94) * mm});
            skLineSegment(sketch, "E3.11.1.0", {"start": v(42.14, 84.86) * mm, "end": v(46.76, 84.86) * mm});
            skLineSegment(sketch, "E3.11.1.1", {"start": v(42.14, 84.86) * mm, "end": v(42.14, 80.24) * mm});
            skLineSegment(sketch, "E3.11.1.2", {"start": v(46.76, 84.86) * mm, "end": v(46.76, 80.24) * mm});
            skLineSegment(sketch, "E3.11.1.3", {"start": v(42.14, 80.24) * mm, "end": v(46.76, 80.24) * mm});
            skLineSegment(sketch, "E3.11.2.0", {"start": v(42.14, 72.16) * mm, "end": v(46.76, 72.16) * mm});
            skLineSegment(sketch, "E3.11.2.1", {"start": v(42.14, 72.16) * mm, "end": v(42.14, 67.54) * mm});
            skLineSegment(sketch, "E3.11.2.2", {"start": v(46.76, 72.16) * mm, "end": v(46.76, 67.54) * mm});
            skLineSegment(sketch, "E3.11.2.3", {"start": v(42.14, 67.54) * mm, "end": v(46.76, 67.54) * mm});
            skLineSegment(sketch, "E3.11.3.0", {"start": v(42.14, 59.46) * mm, "end": v(46.76, 59.46) * mm});
            skLineSegment(sketch, "E3.11.3.1", {"start": v(42.14, 59.46) * mm, "end": v(42.14, 54.84) * mm});
            skLineSegment(sketch, "E3.11.3.2", {"start": v(46.76, 59.46) * mm, "end": v(46.76, 54.84) * mm});
            skLineSegment(sketch, "E3.11.3.3", {"start": v(42.14, 54.84) * mm, "end": v(46.76, 54.84) * mm});
            skLineSegment(sketch, "E3.11.4.0", {"start": v(42.14, 46.76) * mm, "end": v(46.76, 46.76) * mm});
            skLineSegment(sketch, "E3.11.4.1", {"start": v(42.14, 46.76) * mm, "end": v(42.14, 42.14) * mm});
            skLineSegment(sketch, "E3.11.4.2", {"start": v(46.76, 46.76) * mm, "end": v(46.76, 42.14) * mm});
            skLineSegment(sketch, "E3.11.4.3", {"start": v(42.14, 42.14) * mm, "end": v(46.76, 42.14) * mm});
            skLineSegment(sketch, "E3.11.5.0", {"start": v(42.14, 34.06) * mm, "end": v(46.76, 34.06) * mm});
            skLineSegment(sketch, "E3.11.5.1", {"start": v(42.14, 34.06) * mm, "end": v(42.14, 29.44) * mm});
            skLineSegment(sketch, "E3.11.5.2", {"start": v(46.76, 34.06) * mm, "end": v(46.76, 29.44) * mm});
            skLineSegment(sketch, "E3.11.5.3", {"start": v(42.14, 29.44) * mm, "end": v(46.76, 29.44) * mm});
            skLineSegment(sketch, "E3.11.6.0", {"start": v(42.14, 21.36) * mm, "end": v(46.76, 21.36) * mm});
            skLineSegment(sketch, "E3.11.6.1", {"start": v(42.14, 21.36) * mm, "end": v(42.14, 16.74) * mm});
            skLineSegment(sketch, "E3.11.6.2", {"start": v(46.76, 21.36) * mm, "end": v(46.76, 16.74) * mm});
            skLineSegment(sketch, "E3.11.6.3", {"start": v(42.14, 16.74) * mm, "end": v(46.76, 16.74) * mm});
            skLineSegment(sketch, "E3.11.7.0", {"start": v(42.14, 8.66) * mm, "end": v(46.76, 8.66) * mm});
            skLineSegment(sketch, "E3.11.7.1", {"start": v(42.14, 8.66) * mm, "end": v(42.14, 4.04) * mm});
            skLineSegment(sketch, "E3.11.7.2", {"start": v(46.76, 8.66) * mm, "end": v(46.76, 4.04) * mm});
            skLineSegment(sketch, "E3.11.7.3", {"start": v(42.14, 4.04) * mm, "end": v(46.76, 4.04) * mm});
            skLineSegment(sketch, "E3.11.8.0", {"start": v(42.14, -4.04) * mm, "end": v(46.76, -4.04) * mm});
            skLineSegment(sketch, "E3.11.8.1", {"start": v(42.14, -4.04) * mm, "end": v(42.14, -8.66) * mm});
            skLineSegment(sketch, "E3.11.8.2", {"start": v(46.76, -4.04) * mm, "end": v(46.76, -8.66) * mm});
            skLineSegment(sketch, "E3.11.8.3", {"start": v(42.14, -8.66) * mm, "end": v(46.76, -8.66) * mm});
            skLineSegment(sketch, "E3.11.9.0", {"start": v(42.14, -16.74) * mm, "end": v(46.76, -16.74) * mm});
            skLineSegment(sketch, "E3.11.9.1", {"start": v(42.14, -16.74) * mm, "end": v(42.14, -21.36) * mm});
            skLineSegment(sketch, "E3.11.9.2", {"start": v(46.76, -16.74) * mm, "end": v(46.76, -21.36) * mm});
            skLineSegment(sketch, "E3.11.9.3", {"start": v(42.14, -21.36) * mm, "end": v(46.76, -21.36) * mm});
            skLineSegment(sketch, "E3.11.10.0", {"start": v(42.14, -29.44) * mm, "end": v(46.76, -29.44) * mm});
            skLineSegment(sketch, "E3.11.10.1", {"start": v(42.14, -29.44) * mm, "end": v(42.14, -34.06) * mm});
            skLineSegment(sketch, "E3.11.10.2", {"start": v(46.76, -29.44) * mm, "end": v(46.76, -34.06) * mm});
            skLineSegment(sketch, "E3.11.10.3", {"start": v(42.14, -34.06) * mm, "end": v(46.76, -34.06) * mm});
            skLineSegment(sketch, "E3.11.11.0", {"start": v(42.14, -42.14) * mm, "end": v(46.76, -42.14) * mm});
            skLineSegment(sketch, "E3.11.11.1", {"start": v(42.14, -42.14) * mm, "end": v(42.14, -46.76) * mm});
            skLineSegment(sketch, "E3.11.11.2", {"start": v(46.76, -42.14) * mm, "end": v(46.76, -46.76) * mm});
            skLineSegment(sketch, "E3.11.11.3", {"start": v(42.14, -46.76) * mm, "end": v(46.76, -46.76) * mm});
            skLineSegment(sketch, "E3.11.12.0", {"start": v(42.14, -54.84) * mm, "end": v(46.76, -54.84) * mm});
            skLineSegment(sketch, "E3.11.12.1", {"start": v(42.14, -54.84) * mm, "end": v(42.14, -59.46) * mm});
            skLineSegment(sketch, "E3.11.12.2", {"start": v(46.76, -54.84) * mm, "end": v(46.76, -59.46) * mm});
            skLineSegment(sketch, "E3.11.12.3", {"start": v(42.14, -59.46) * mm, "end": v(46.76, -59.46) * mm});
            skLineSegment(sketch, "E3.11.13.0", {"start": v(42.14, -67.54) * mm, "end": v(46.76, -67.54) * mm});
            skLineSegment(sketch, "E3.11.13.1", {"start": v(42.14, -67.54) * mm, "end": v(42.14, -72.16) * mm});
            skLineSegment(sketch, "E3.11.13.2", {"start": v(46.76, -67.54) * mm, "end": v(46.76, -72.16) * mm});
            skLineSegment(sketch, "E3.11.13.3", {"start": v(42.14, -72.16) * mm, "end": v(46.76, -72.16) * mm});
            skLineSegment(sketch, "E3.11.14.0", {"start": v(42.14, -80.24) * mm, "end": v(46.76, -80.24) * mm});
            skLineSegment(sketch, "E3.11.14.1", {"start": v(42.14, -80.24) * mm, "end": v(42.14, -84.86) * mm});
            skLineSegment(sketch, "E3.11.14.2", {"start": v(46.76, -80.24) * mm, "end": v(46.76, -84.86) * mm});
            skLineSegment(sketch, "E3.11.14.3", {"start": v(42.14, -84.86) * mm, "end": v(46.76, -84.86) * mm});
            skLineSegment(sketch, "E3.11.15.0", {"start": v(42.14, -92.94) * mm, "end": v(46.76, -92.94) * mm});
            skLineSegment(sketch, "E3.11.15.1", {"start": v(42.14, -92.94) * mm, "end": v(42.14, -97.56) * mm});
            skLineSegment(sketch, "E3.11.15.2", {"start": v(46.76, -92.94) * mm, "end": v(46.76, -97.56) * mm});
            skLineSegment(sketch, "E3.11.15.3", {"start": v(42.14, -97.56) * mm, "end": v(46.76, -97.56) * mm});
            skLineSegment(sketch, "E3.11.16.0", {"start": v(42.14, -105.64) * mm, "end": v(46.76, -105.64) * mm});
            skLineSegment(sketch, "E3.11.16.1", {"start": v(42.14, -105.64) * mm, "end": v(42.14, -110.26) * mm});
            skLineSegment(sketch, "E3.11.16.2", {"start": v(46.76, -105.64) * mm, "end": v(46.76, -110.26) * mm});
            skLineSegment(sketch, "E3.11.16.3", {"start": v(42.14, -110.26) * mm, "end": v(46.76, -110.26) * mm});
            skLineSegment(sketch, "E3.12.0.0", {"start": v(54.84, 97.56) * mm, "end": v(59.46, 97.56) * mm});
            skLineSegment(sketch, "E3.12.0.1", {"start": v(54.84, 97.56) * mm, "end": v(54.84, 92.94) * mm});
            skLineSegment(sketch, "E3.12.0.2", {"start": v(59.46, 97.56) * mm, "end": v(59.46, 92.94) * mm});
            skLineSegment(sketch, "E3.12.0.3", {"start": v(54.84, 92.94) * mm, "end": v(59.46, 92.94) * mm});
            skLineSegment(sketch, "E3.12.1.0", {"start": v(54.84, 84.86) * mm, "end": v(59.46, 84.86) * mm});
            skLineSegment(sketch, "E3.12.1.1", {"start": v(54.84, 84.86) * mm, "end": v(54.84, 80.24) * mm});
            skLineSegment(sketch, "E3.12.1.2", {"start": v(59.46, 84.86) * mm, "end": v(59.46, 80.24) * mm});
            skLineSegment(sketch, "E3.12.1.3", {"start": v(54.84, 80.24) * mm, "end": v(59.46, 80.24) * mm});
            skLineSegment(sketch, "E3.12.2.0", {"start": v(54.84, 72.16) * mm, "end": v(59.46, 72.16) * mm});
            skLineSegment(sketch, "E3.12.2.1", {"start": v(54.84, 72.16) * mm, "end": v(54.84, 67.54) * mm});
            skLineSegment(sketch, "E3.12.2.2", {"start": v(59.46, 72.16) * mm, "end": v(59.46, 67.54) * mm});
            skLineSegment(sketch, "E3.12.2.3", {"start": v(54.84, 67.54) * mm, "end": v(59.46, 67.54) * mm});
            skLineSegment(sketch, "E3.12.3.0", {"start": v(54.84, 59.46) * mm, "end": v(59.46, 59.46) * mm});
            skLineSegment(sketch, "E3.12.3.1", {"start": v(54.84, 59.46) * mm, "end": v(54.84, 54.84) * mm});
            skLineSegment(sketch, "E3.12.3.2", {"start": v(59.46, 59.46) * mm, "end": v(59.46, 54.84) * mm});
            skLineSegment(sketch, "E3.12.3.3", {"start": v(54.84, 54.84) * mm, "end": v(59.46, 54.84) * mm});
            skLineSegment(sketch, "E3.12.4.0", {"start": v(54.84, 46.76) * mm, "end": v(59.46, 46.76) * mm});
            skLineSegment(sketch, "E3.12.4.1", {"start": v(54.84, 46.76) * mm, "end": v(54.84, 42.14) * mm});
            skLineSegment(sketch, "E3.12.4.2", {"start": v(59.46, 46.76) * mm, "end": v(59.46, 42.14) * mm});
            skLineSegment(sketch, "E3.12.4.3", {"start": v(54.84, 42.14) * mm, "end": v(59.46, 42.14) * mm});
            skLineSegment(sketch, "E3.12.5.0", {"start": v(54.84, 34.06) * mm, "end": v(59.46, 34.06) * mm});
            skLineSegment(sketch, "E3.12.5.1", {"start": v(54.84, 34.06) * mm, "end": v(54.84, 29.44) * mm});
            skLineSegment(sketch, "E3.12.5.2", {"start": v(59.46, 34.06) * mm, "end": v(59.46, 29.44) * mm});
            skLineSegment(sketch, "E3.12.5.3", {"start": v(54.84, 29.44) * mm, "end": v(59.46, 29.44) * mm});
            skLineSegment(sketch, "E3.12.6.0", {"start": v(54.84, 21.36) * mm, "end": v(59.46, 21.36) * mm});
            skLineSegment(sketch, "E3.12.6.1", {"start": v(54.84, 21.36) * mm, "end": v(54.84, 16.74) * mm});
            skLineSegment(sketch, "E3.12.6.2", {"start": v(59.46, 21.36) * mm, "end": v(59.46, 16.74) * mm});
            skLineSegment(sketch, "E3.12.6.3", {"start": v(54.84, 16.74) * mm, "end": v(59.46, 16.74) * mm});
            skLineSegment(sketch, "E3.12.7.0", {"start": v(54.84, 8.66) * mm, "end": v(59.46, 8.66) * mm});
            skLineSegment(sketch, "E3.12.7.1", {"start": v(54.84, 8.66) * mm, "end": v(54.84, 4.04) * mm});
            skLineSegment(sketch, "E3.12.7.2", {"start": v(59.46, 8.66) * mm, "end": v(59.46, 4.04) * mm});
            skLineSegment(sketch, "E3.12.7.3", {"start": v(54.84, 4.04) * mm, "end": v(59.46, 4.04) * mm});
            skLineSegment(sketch, "E3.12.8.0", {"start": v(54.84, -4.04) * mm, "end": v(59.46, -4.04) * mm});
            skLineSegment(sketch, "E3.12.8.1", {"start": v(54.84, -4.04) * mm, "end": v(54.84, -8.66) * mm});
            skLineSegment(sketch, "E3.12.8.2", {"start": v(59.46, -4.04) * mm, "end": v(59.46, -8.66) * mm});
            skLineSegment(sketch, "E3.12.8.3", {"start": v(54.84, -8.66) * mm, "end": v(59.46, -8.66) * mm});
            skLineSegment(sketch, "E3.12.9.0", {"start": v(54.84, -16.74) * mm, "end": v(59.46, -16.74) * mm});
            skLineSegment(sketch, "E3.12.9.1", {"start": v(54.84, -16.74) * mm, "end": v(54.84, -21.36) * mm});
            skLineSegment(sketch, "E3.12.9.2", {"start": v(59.46, -16.74) * mm, "end": v(59.46, -21.36) * mm});
            skLineSegment(sketch, "E3.12.9.3", {"start": v(54.84, -21.36) * mm, "end": v(59.46, -21.36) * mm});
            skLineSegment(sketch, "E3.12.10.0", {"start": v(54.84, -29.44) * mm, "end": v(59.46, -29.44) * mm});
            skLineSegment(sketch, "E3.12.10.1", {"start": v(54.84, -29.44) * mm, "end": v(54.84, -34.06) * mm});
            skLineSegment(sketch, "E3.12.10.2", {"start": v(59.46, -29.44) * mm, "end": v(59.46, -34.06) * mm});
            skLineSegment(sketch, "E3.12.10.3", {"start": v(54.84, -34.06) * mm, "end": v(59.46, -34.06) * mm});
            skLineSegment(sketch, "E3.12.11.0", {"start": v(54.84, -42.14) * mm, "end": v(59.46, -42.14) * mm});
            skLineSegment(sketch, "E3.12.11.1", {"start": v(54.84, -42.14) * mm, "end": v(54.84, -46.76) * mm});
            skLineSegment(sketch, "E3.12.11.2", {"start": v(59.46, -42.14) * mm, "end": v(59.46, -46.76) * mm});
            skLineSegment(sketch, "E3.12.11.3", {"start": v(54.84, -46.76) * mm, "end": v(59.46, -46.76) * mm});
            skLineSegment(sketch, "E3.12.12.0", {"start": v(54.84, -54.84) * mm, "end": v(59.46, -54.84) * mm});
            skLineSegment(sketch, "E3.12.12.1", {"start": v(54.84, -54.84) * mm, "end": v(54.84, -59.46) * mm});
            skLineSegment(sketch, "E3.12.12.2", {"start": v(59.46, -54.84) * mm, "end": v(59.46, -59.46) * mm});
            skLineSegment(sketch, "E3.12.12.3", {"start": v(54.84, -59.46) * mm, "end": v(59.46, -59.46) * mm});
            skLineSegment(sketch, "E3.12.13.0", {"start": v(54.84, -67.54) * mm, "end": v(59.46, -67.54) * mm});
            skLineSegment(sketch, "E3.12.13.1", {"start": v(54.84, -67.54) * mm, "end": v(54.84, -72.16) * mm});
            skLineSegment(sketch, "E3.12.13.2", {"start": v(59.46, -67.54) * mm, "end": v(59.46, -72.16) * mm});
            skLineSegment(sketch, "E3.12.13.3", {"start": v(54.84, -72.16) * mm, "end": v(59.46, -72.16) * mm});
            skLineSegment(sketch, "E3.12.14.0", {"start": v(54.84, -80.24) * mm, "end": v(59.46, -80.24) * mm});
            skLineSegment(sketch, "E3.12.14.1", {"start": v(54.84, -80.24) * mm, "end": v(54.84, -84.86) * mm});
            skLineSegment(sketch, "E3.12.14.2", {"start": v(59.46, -80.24) * mm, "end": v(59.46, -84.86) * mm});
            skLineSegment(sketch, "E3.12.14.3", {"start": v(54.84, -84.86) * mm, "end": v(59.46, -84.86) * mm});
            skLineSegment(sketch, "E3.12.15.0", {"start": v(54.84, -92.94) * mm, "end": v(59.46, -92.94) * mm});
            skLineSegment(sketch, "E3.12.15.1", {"start": v(54.84, -92.94) * mm, "end": v(54.84, -97.56) * mm});
            skLineSegment(sketch, "E3.12.15.2", {"start": v(59.46, -92.94) * mm, "end": v(59.46, -97.56) * mm});
            skLineSegment(sketch, "E3.12.15.3", {"start": v(54.84, -97.56) * mm, "end": v(59.46, -97.56) * mm});
            skLineSegment(sketch, "E3.12.16.0", {"start": v(54.84, -105.64) * mm, "end": v(59.46, -105.64) * mm});
            skLineSegment(sketch, "E3.12.16.1", {"start": v(54.84, -105.64) * mm, "end": v(54.84, -110.26) * mm});
            skLineSegment(sketch, "E3.12.16.2", {"start": v(59.46, -105.64) * mm, "end": v(59.46, -110.26) * mm});
            skLineSegment(sketch, "E3.12.16.3", {"start": v(54.84, -110.26) * mm, "end": v(59.46, -110.26) * mm});
            skLineSegment(sketch, "E3.13.0.0", {"start": v(67.54, 97.56) * mm, "end": v(72.16, 97.56) * mm});
            skLineSegment(sketch, "E3.13.0.1", {"start": v(67.54, 97.56) * mm, "end": v(67.54, 92.94) * mm});
            skLineSegment(sketch, "E3.13.0.2", {"start": v(72.16, 97.56) * mm, "end": v(72.16, 92.94) * mm});
            skLineSegment(sketch, "E3.13.0.3", {"start": v(67.54, 92.94) * mm, "end": v(72.16, 92.94) * mm});
            skLineSegment(sketch, "E3.13.1.0", {"start": v(67.54, 84.86) * mm, "end": v(72.16, 84.86) * mm});
            skLineSegment(sketch, "E3.13.1.1", {"start": v(67.54, 84.86) * mm, "end": v(67.54, 80.24) * mm});
            skLineSegment(sketch, "E3.13.1.2", {"start": v(72.16, 84.86) * mm, "end": v(72.16, 80.24) * mm});
            skLineSegment(sketch, "E3.13.1.3", {"start": v(67.54, 80.24) * mm, "end": v(72.16, 80.24) * mm});
            skLineSegment(sketch, "E3.13.2.0", {"start": v(67.54, 72.16) * mm, "end": v(72.16, 72.16) * mm});
            skLineSegment(sketch, "E3.13.2.1", {"start": v(67.54, 72.16) * mm, "end": v(67.54, 67.54) * mm});
            skLineSegment(sketch, "E3.13.2.2", {"start": v(72.16, 72.16) * mm, "end": v(72.16, 67.54) * mm});
            skLineSegment(sketch, "E3.13.2.3", {"start": v(67.54, 67.54) * mm, "end": v(72.16, 67.54) * mm});
            skLineSegment(sketch, "E3.13.3.0", {"start": v(67.54, 59.46) * mm, "end": v(72.16, 59.46) * mm});
            skLineSegment(sketch, "E3.13.3.1", {"start": v(67.54, 59.46) * mm, "end": v(67.54, 54.84) * mm});
            skLineSegment(sketch, "E3.13.3.2", {"start": v(72.16, 59.46) * mm, "end": v(72.16, 54.84) * mm});
            skLineSegment(sketch, "E3.13.3.3", {"start": v(67.54, 54.84) * mm, "end": v(72.16, 54.84) * mm});
            skLineSegment(sketch, "E3.13.4.0", {"start": v(67.54, 46.76) * mm, "end": v(72.16, 46.76) * mm});
            skLineSegment(sketch, "E3.13.4.1", {"start": v(67.54, 46.76) * mm, "end": v(67.54, 42.14) * mm});
            skLineSegment(sketch, "E3.13.4.2", {"start": v(72.16, 46.76) * mm, "end": v(72.16, 42.14) * mm});
            skLineSegment(sketch, "E3.13.4.3", {"start": v(67.54, 42.14) * mm, "end": v(72.16, 42.14) * mm});
            skLineSegment(sketch, "E3.13.5.0", {"start": v(67.54, 34.06) * mm, "end": v(72.16, 34.06) * mm});
            skLineSegment(sketch, "E3.13.5.1", {"start": v(67.54, 34.06) * mm, "end": v(67.54, 29.44) * mm});
            skLineSegment(sketch, "E3.13.5.2", {"start": v(72.16, 34.06) * mm, "end": v(72.16, 29.44) * mm});
            skLineSegment(sketch, "E3.13.5.3", {"start": v(67.54, 29.44) * mm, "end": v(72.16, 29.44) * mm});
            skLineSegment(sketch, "E3.13.6.0", {"start": v(67.54, 21.36) * mm, "end": v(72.16, 21.36) * mm});
            skLineSegment(sketch, "E3.13.6.1", {"start": v(67.54, 21.36) * mm, "end": v(67.54, 16.74) * mm});
            skLineSegment(sketch, "E3.13.6.2", {"start": v(72.16, 21.36) * mm, "end": v(72.16, 16.74) * mm});
            skLineSegment(sketch, "E3.13.6.3", {"start": v(67.54, 16.74) * mm, "end": v(72.16, 16.74) * mm});
            skLineSegment(sketch, "E3.13.7.0", {"start": v(67.54, 8.66) * mm, "end": v(72.16, 8.66) * mm});
            skLineSegment(sketch, "E3.13.7.1", {"start": v(67.54, 8.66) * mm, "end": v(67.54, 4.04) * mm});
            skLineSegment(sketch, "E3.13.7.2", {"start": v(72.16, 8.66) * mm, "end": v(72.16, 4.04) * mm});
            skLineSegment(sketch, "E3.13.7.3", {"start": v(67.54, 4.04) * mm, "end": v(72.16, 4.04) * mm});
            skLineSegment(sketch, "E3.13.8.0", {"start": v(67.54, -4.04) * mm, "end": v(72.16, -4.04) * mm});
            skLineSegment(sketch, "E3.13.8.1", {"start": v(67.54, -4.04) * mm, "end": v(67.54, -8.66) * mm});
            skLineSegment(sketch, "E3.13.8.2", {"start": v(72.16, -4.04) * mm, "end": v(72.16, -8.66) * mm});
            skLineSegment(sketch, "E3.13.8.3", {"start": v(67.54, -8.66) * mm, "end": v(72.16, -8.66) * mm});
            skLineSegment(sketch, "E3.13.9.0", {"start": v(67.54, -16.74) * mm, "end": v(72.16, -16.74) * mm});
            skLineSegment(sketch, "E3.13.9.1", {"start": v(67.54, -16.74) * mm, "end": v(67.54, -21.36) * mm});
            skLineSegment(sketch, "E3.13.9.2", {"start": v(72.16, -16.74) * mm, "end": v(72.16, -21.36) * mm});
            skLineSegment(sketch, "E3.13.9.3", {"start": v(67.54, -21.36) * mm, "end": v(72.16, -21.36) * mm});
            skLineSegment(sketch, "E3.13.10.0", {"start": v(67.54, -29.44) * mm, "end": v(72.16, -29.44) * mm});
            skLineSegment(sketch, "E3.13.10.1", {"start": v(67.54, -29.44) * mm, "end": v(67.54, -34.06) * mm});
            skLineSegment(sketch, "E3.13.10.2", {"start": v(72.16, -29.44) * mm, "end": v(72.16, -34.06) * mm});
            skLineSegment(sketch, "E3.13.10.3", {"start": v(67.54, -34.06) * mm, "end": v(72.16, -34.06) * mm});
            skLineSegment(sketch, "E3.13.11.0", {"start": v(67.54, -42.14) * mm, "end": v(72.16, -42.14) * mm});
            skLineSegment(sketch, "E3.13.11.1", {"start": v(67.54, -42.14) * mm, "end": v(67.54, -46.76) * mm});
            skLineSegment(sketch, "E3.13.11.2", {"start": v(72.16, -42.14) * mm, "end": v(72.16, -46.76) * mm});
            skLineSegment(sketch, "E3.13.11.3", {"start": v(67.54, -46.76) * mm, "end": v(72.16, -46.76) * mm});
            skLineSegment(sketch, "E3.13.12.0", {"start": v(67.54, -54.84) * mm, "end": v(72.16, -54.84) * mm});
            skLineSegment(sketch, "E3.13.12.1", {"start": v(67.54, -54.84) * mm, "end": v(67.54, -59.46) * mm});
            skLineSegment(sketch, "E3.13.12.2", {"start": v(72.16, -54.84) * mm, "end": v(72.16, -59.46) * mm});
            skLineSegment(sketch, "E3.13.12.3", {"start": v(67.54, -59.46) * mm, "end": v(72.16, -59.46) * mm});
            skLineSegment(sketch, "E3.13.13.0", {"start": v(67.54, -67.54) * mm, "end": v(72.16, -67.54) * mm});
            skLineSegment(sketch, "E3.13.13.1", {"start": v(67.54, -67.54) * mm, "end": v(67.54, -72.16) * mm});
            skLineSegment(sketch, "E3.13.13.2", {"start": v(72.16, -67.54) * mm, "end": v(72.16, -72.16) * mm});
            skLineSegment(sketch, "E3.13.13.3", {"start": v(67.54, -72.16) * mm, "end": v(72.16, -72.16) * mm});
            skLineSegment(sketch, "E3.13.14.0", {"start": v(67.54, -80.24) * mm, "end": v(72.16, -80.24) * mm});
            skLineSegment(sketch, "E3.13.14.1", {"start": v(67.54, -80.24) * mm, "end": v(67.54, -84.86) * mm});
            skLineSegment(sketch, "E3.13.14.2", {"start": v(72.16, -80.24) * mm, "end": v(72.16, -84.86) * mm});
            skLineSegment(sketch, "E3.13.14.3", {"start": v(67.54, -84.86) * mm, "end": v(72.16, -84.86) * mm});
            skLineSegment(sketch, "E3.13.15.0", {"start": v(67.54, -92.94) * mm, "end": v(72.16, -92.94) * mm});
            skLineSegment(sketch, "E3.13.15.1", {"start": v(67.54, -92.94) * mm, "end": v(67.54, -97.56) * mm});
            skLineSegment(sketch, "E3.13.15.2", {"start": v(72.16, -92.94) * mm, "end": v(72.16, -97.56) * mm});
            skLineSegment(sketch, "E3.13.15.3", {"start": v(67.54, -97.56) * mm, "end": v(72.16, -97.56) * mm});
            skLineSegment(sketch, "E3.13.16.0", {"start": v(67.54, -105.64) * mm, "end": v(72.16, -105.64) * mm});
            skLineSegment(sketch, "E3.13.16.1", {"start": v(67.54, -105.64) * mm, "end": v(67.54, -110.26) * mm});
            skLineSegment(sketch, "E3.13.16.2", {"start": v(72.16, -105.64) * mm, "end": v(72.16, -110.26) * mm});
            skLineSegment(sketch, "E3.13.16.3", {"start": v(67.54, -110.26) * mm, "end": v(72.16, -110.26) * mm});
            skLineSegment(sketch, "E3.14.0.0", {"start": v(80.24, 97.56) * mm, "end": v(84.86, 97.56) * mm});
            skLineSegment(sketch, "E3.14.0.1", {"start": v(80.24, 97.56) * mm, "end": v(80.24, 92.94) * mm});
            skLineSegment(sketch, "E3.14.0.2", {"start": v(84.86, 97.56) * mm, "end": v(84.86, 92.94) * mm});
            skLineSegment(sketch, "E3.14.0.3", {"start": v(80.24, 92.94) * mm, "end": v(84.86, 92.94) * mm});
            skLineSegment(sketch, "E3.14.1.0", {"start": v(80.24, 84.86) * mm, "end": v(84.86, 84.86) * mm});
            skLineSegment(sketch, "E3.14.1.1", {"start": v(80.24, 84.86) * mm, "end": v(80.24, 80.24) * mm});
            skLineSegment(sketch, "E3.14.1.2", {"start": v(84.86, 84.86) * mm, "end": v(84.86, 80.24) * mm});
            skLineSegment(sketch, "E3.14.1.3", {"start": v(80.24, 80.24) * mm, "end": v(84.86, 80.24) * mm});
            skLineSegment(sketch, "E3.14.2.0", {"start": v(80.24, 72.16) * mm, "end": v(84.86, 72.16) * mm});
            skLineSegment(sketch, "E3.14.2.1", {"start": v(80.24, 72.16) * mm, "end": v(80.24, 67.54) * mm});
            skLineSegment(sketch, "E3.14.2.2", {"start": v(84.86, 72.16) * mm, "end": v(84.86, 67.54) * mm});
            skLineSegment(sketch, "E3.14.2.3", {"start": v(80.24, 67.54) * mm, "end": v(84.86, 67.54) * mm});
            skLineSegment(sketch, "E3.14.3.0", {"start": v(80.24, 59.46) * mm, "end": v(84.86, 59.46) * mm});
            skLineSegment(sketch, "E3.14.3.1", {"start": v(80.24, 59.46) * mm, "end": v(80.24, 54.84) * mm});
            skLineSegment(sketch, "E3.14.3.2", {"start": v(84.86, 59.46) * mm, "end": v(84.86, 54.84) * mm});
            skLineSegment(sketch, "E3.14.3.3", {"start": v(80.24, 54.84) * mm, "end": v(84.86, 54.84) * mm});
            skLineSegment(sketch, "E3.14.4.0", {"start": v(80.24, 46.76) * mm, "end": v(84.86, 46.76) * mm});
            skLineSegment(sketch, "E3.14.4.1", {"start": v(80.24, 46.76) * mm, "end": v(80.24, 42.14) * mm});
            skLineSegment(sketch, "E3.14.4.2", {"start": v(84.86, 46.76) * mm, "end": v(84.86, 42.14) * mm});
            skLineSegment(sketch, "E3.14.4.3", {"start": v(80.24, 42.14) * mm, "end": v(84.86, 42.14) * mm});
            skLineSegment(sketch, "E3.14.5.0", {"start": v(80.24, 34.06) * mm, "end": v(84.86, 34.06) * mm});
            skLineSegment(sketch, "E3.14.5.1", {"start": v(80.24, 34.06) * mm, "end": v(80.24, 29.44) * mm});
            skLineSegment(sketch, "E3.14.5.2", {"start": v(84.86, 34.06) * mm, "end": v(84.86, 29.44) * mm});
            skLineSegment(sketch, "E3.14.5.3", {"start": v(80.24, 29.44) * mm, "end": v(84.86, 29.44) * mm});
            skLineSegment(sketch, "E3.14.6.0", {"start": v(80.24, 21.36) * mm, "end": v(84.86, 21.36) * mm});
            skLineSegment(sketch, "E3.14.6.1", {"start": v(80.24, 21.36) * mm, "end": v(80.24, 16.74) * mm});
            skLineSegment(sketch, "E3.14.6.2", {"start": v(84.86, 21.36) * mm, "end": v(84.86, 16.74) * mm});
            skLineSegment(sketch, "E3.14.6.3", {"start": v(80.24, 16.74) * mm, "end": v(84.86, 16.74) * mm});
            skLineSegment(sketch, "E3.14.7.0", {"start": v(80.24, 8.66) * mm, "end": v(84.86, 8.66) * mm});
            skLineSegment(sketch, "E3.14.7.1", {"start": v(80.24, 8.66) * mm, "end": v(80.24, 4.04) * mm});
            skLineSegment(sketch, "E3.14.7.2", {"start": v(84.86, 8.66) * mm, "end": v(84.86, 4.04) * mm});
            skLineSegment(sketch, "E3.14.7.3", {"start": v(80.24, 4.04) * mm, "end": v(84.86, 4.04) * mm});
            skLineSegment(sketch, "E3.14.8.0", {"start": v(80.24, -4.04) * mm, "end": v(84.86, -4.04) * mm});
            skLineSegment(sketch, "E3.14.8.1", {"start": v(80.24, -4.04) * mm, "end": v(80.24, -8.66) * mm});
            skLineSegment(sketch, "E3.14.8.2", {"start": v(84.86, -4.04) * mm, "end": v(84.86, -8.66) * mm});
            skLineSegment(sketch, "E3.14.8.3", {"start": v(80.24, -8.66) * mm, "end": v(84.86, -8.66) * mm});
            skLineSegment(sketch, "E3.14.9.0", {"start": v(80.24, -16.74) * mm, "end": v(84.86, -16.74) * mm});
            skLineSegment(sketch, "E3.14.9.1", {"start": v(80.24, -16.74) * mm, "end": v(80.24, -21.36) * mm});
            skLineSegment(sketch, "E3.14.9.2", {"start": v(84.86, -16.74) * mm, "end": v(84.86, -21.36) * mm});
            skLineSegment(sketch, "E3.14.9.3", {"start": v(80.24, -21.36) * mm, "end": v(84.86, -21.36) * mm});
            skLineSegment(sketch, "E3.14.10.0", {"start": v(80.24, -29.44) * mm, "end": v(84.86, -29.44) * mm});
            skLineSegment(sketch, "E3.14.10.1", {"start": v(80.24, -29.44) * mm, "end": v(80.24, -34.06) * mm});
            skLineSegment(sketch, "E3.14.10.2", {"start": v(84.86, -29.44) * mm, "end": v(84.86, -34.06) * mm});
            skLineSegment(sketch, "E3.14.10.3", {"start": v(80.24, -34.06) * mm, "end": v(84.86, -34.06) * mm});
            skLineSegment(sketch, "E3.14.11.0", {"start": v(80.24, -42.14) * mm, "end": v(84.86, -42.14) * mm});
            skLineSegment(sketch, "E3.14.11.1", {"start": v(80.24, -42.14) * mm, "end": v(80.24, -46.76) * mm});
            skLineSegment(sketch, "E3.14.11.2", {"start": v(84.86, -42.14) * mm, "end": v(84.86, -46.76) * mm});
            skLineSegment(sketch, "E3.14.11.3", {"start": v(80.24, -46.76) * mm, "end": v(84.86, -46.76) * mm});
            skLineSegment(sketch, "E3.14.12.0", {"start": v(80.24, -54.84) * mm, "end": v(84.86, -54.84) * mm});
            skLineSegment(sketch, "E3.14.12.1", {"start": v(80.24, -54.84) * mm, "end": v(80.24, -59.46) * mm});
            skLineSegment(sketch, "E3.14.12.2", {"start": v(84.86, -54.84) * mm, "end": v(84.86, -59.46) * mm});
            skLineSegment(sketch, "E3.14.12.3", {"start": v(80.24, -59.46) * mm, "end": v(84.86, -59.46) * mm});
            skLineSegment(sketch, "E3.14.13.0", {"start": v(80.24, -67.54) * mm, "end": v(84.86, -67.54) * mm});
            skLineSegment(sketch, "E3.14.13.1", {"start": v(80.24, -67.54) * mm, "end": v(80.24, -72.16) * mm});
            skLineSegment(sketch, "E3.14.13.2", {"start": v(84.86, -67.54) * mm, "end": v(84.86, -72.16) * mm});
            skLineSegment(sketch, "E3.14.13.3", {"start": v(80.24, -72.16) * mm, "end": v(84.86, -72.16) * mm});
            skLineSegment(sketch, "E3.14.14.0", {"start": v(80.24, -80.24) * mm, "end": v(84.86, -80.24) * mm});
            skLineSegment(sketch, "E3.14.14.1", {"start": v(80.24, -80.24) * mm, "end": v(80.24, -84.86) * mm});
            skLineSegment(sketch, "E3.14.14.2", {"start": v(84.86, -80.24) * mm, "end": v(84.86, -84.86) * mm});
            skLineSegment(sketch, "E3.14.14.3", {"start": v(80.24, -84.86) * mm, "end": v(84.86, -84.86) * mm});
            skLineSegment(sketch, "E3.14.15.0", {"start": v(80.24, -92.94) * mm, "end": v(84.86, -92.94) * mm});
            skLineSegment(sketch, "E3.14.15.1", {"start": v(80.24, -92.94) * mm, "end": v(80.24, -97.56) * mm});
            skLineSegment(sketch, "E3.14.15.2", {"start": v(84.86, -92.94) * mm, "end": v(84.86, -97.56) * mm});
            skLineSegment(sketch, "E3.14.15.3", {"start": v(80.24, -97.56) * mm, "end": v(84.86, -97.56) * mm});
            skLineSegment(sketch, "E3.14.16.0", {"start": v(80.24, -105.64) * mm, "end": v(84.86, -105.64) * mm});
            skLineSegment(sketch, "E3.14.16.1", {"start": v(80.24, -105.64) * mm, "end": v(80.24, -110.26) * mm});
            skLineSegment(sketch, "E3.14.16.2", {"start": v(84.86, -105.64) * mm, "end": v(84.86, -110.26) * mm});
            skLineSegment(sketch, "E3.14.16.3", {"start": v(80.24, -110.26) * mm, "end": v(84.86, -110.26) * mm});
            skLineSegment(sketch, "E3.15.0.0", {"start": v(92.94, 97.56) * mm, "end": v(97.56, 97.56) * mm});
            skLineSegment(sketch, "E3.15.0.1", {"start": v(92.94, 97.56) * mm, "end": v(92.94, 92.94) * mm});
            skLineSegment(sketch, "E3.15.0.2", {"start": v(97.56, 97.56) * mm, "end": v(97.56, 92.94) * mm});
            skLineSegment(sketch, "E3.15.0.3", {"start": v(92.94, 92.94) * mm, "end": v(97.56, 92.94) * mm});
            skLineSegment(sketch, "E3.15.1.0", {"start": v(92.94, 84.86) * mm, "end": v(97.56, 84.86) * mm});
            skLineSegment(sketch, "E3.15.1.1", {"start": v(92.94, 84.86) * mm, "end": v(92.94, 80.24) * mm});
            skLineSegment(sketch, "E3.15.1.2", {"start": v(97.56, 84.86) * mm, "end": v(97.56, 80.24) * mm});
            skLineSegment(sketch, "E3.15.1.3", {"start": v(92.94, 80.24) * mm, "end": v(97.56, 80.24) * mm});
            skLineSegment(sketch, "E3.15.2.0", {"start": v(92.94, 72.16) * mm, "end": v(97.56, 72.16) * mm});
            skLineSegment(sketch, "E3.15.2.1", {"start": v(92.94, 72.16) * mm, "end": v(92.94, 67.54) * mm});
            skLineSegment(sketch, "E3.15.2.2", {"start": v(97.56, 72.16) * mm, "end": v(97.56, 67.54) * mm});
            skLineSegment(sketch, "E3.15.2.3", {"start": v(92.94, 67.54) * mm, "end": v(97.56, 67.54) * mm});
            skLineSegment(sketch, "E3.15.3.0", {"start": v(92.94, 59.46) * mm, "end": v(97.56, 59.46) * mm});
            skLineSegment(sketch, "E3.15.3.1", {"start": v(92.94, 59.46) * mm, "end": v(92.94, 54.84) * mm});
            skLineSegment(sketch, "E3.15.3.2", {"start": v(97.56, 59.46) * mm, "end": v(97.56, 54.84) * mm});
            skLineSegment(sketch, "E3.15.3.3", {"start": v(92.94, 54.84) * mm, "end": v(97.56, 54.84) * mm});
            skLineSegment(sketch, "E3.15.4.0", {"start": v(92.94, 46.76) * mm, "end": v(97.56, 46.76) * mm});
            skLineSegment(sketch, "E3.15.4.1", {"start": v(92.94, 46.76) * mm, "end": v(92.94, 42.14) * mm});
            skLineSegment(sketch, "E3.15.4.2", {"start": v(97.56, 46.76) * mm, "end": v(97.56, 42.14) * mm});
            skLineSegment(sketch, "E3.15.4.3", {"start": v(92.94, 42.14) * mm, "end": v(97.56, 42.14) * mm});
            skLineSegment(sketch, "E3.15.5.0", {"start": v(92.94, 34.06) * mm, "end": v(97.56, 34.06) * mm});
            skLineSegment(sketch, "E3.15.5.1", {"start": v(92.94, 34.06) * mm, "end": v(92.94, 29.44) * mm});
            skLineSegment(sketch, "E3.15.5.2", {"start": v(97.56, 34.06) * mm, "end": v(97.56, 29.44) * mm});
            skLineSegment(sketch, "E3.15.5.3", {"start": v(92.94, 29.44) * mm, "end": v(97.56, 29.44) * mm});
            skLineSegment(sketch, "E3.15.6.0", {"start": v(92.94, 21.36) * mm, "end": v(97.56, 21.36) * mm});
            skLineSegment(sketch, "E3.15.6.1", {"start": v(92.94, 21.36) * mm, "end": v(92.94, 16.74) * mm});
            skLineSegment(sketch, "E3.15.6.2", {"start": v(97.56, 21.36) * mm, "end": v(97.56, 16.74) * mm});
            skLineSegment(sketch, "E3.15.6.3", {"start": v(92.94, 16.74) * mm, "end": v(97.56, 16.74) * mm});
            skLineSegment(sketch, "E3.15.7.0", {"start": v(92.94, 8.66) * mm, "end": v(97.56, 8.66) * mm});
            skLineSegment(sketch, "E3.15.7.1", {"start": v(92.94, 8.66) * mm, "end": v(92.94, 4.04) * mm});
            skLineSegment(sketch, "E3.15.7.2", {"start": v(97.56, 8.66) * mm, "end": v(97.56, 4.04) * mm});
            skLineSegment(sketch, "E3.15.7.3", {"start": v(92.94, 4.04) * mm, "end": v(97.56, 4.04) * mm});
            skLineSegment(sketch, "E3.15.8.0", {"start": v(92.94, -4.04) * mm, "end": v(97.56, -4.04) * mm});
            skLineSegment(sketch, "E3.15.8.1", {"start": v(92.94, -4.04) * mm, "end": v(92.94, -8.66) * mm});
            skLineSegment(sketch, "E3.15.8.2", {"start": v(97.56, -4.04) * mm, "end": v(97.56, -8.66) * mm});
            skLineSegment(sketch, "E3.15.8.3", {"start": v(92.94, -8.66) * mm, "end": v(97.56, -8.66) * mm});
            skLineSegment(sketch, "E3.15.9.0", {"start": v(92.94, -16.74) * mm, "end": v(97.56, -16.74) * mm});
            skLineSegment(sketch, "E3.15.9.1", {"start": v(92.94, -16.74) * mm, "end": v(92.94, -21.36) * mm});
            skLineSegment(sketch, "E3.15.9.2", {"start": v(97.56, -16.74) * mm, "end": v(97.56, -21.36) * mm});
            skLineSegment(sketch, "E3.15.9.3", {"start": v(92.94, -21.36) * mm, "end": v(97.56, -21.36) * mm});
            skLineSegment(sketch, "E3.15.10.0", {"start": v(92.94, -29.44) * mm, "end": v(97.56, -29.44) * mm});
            skLineSegment(sketch, "E3.15.10.1", {"start": v(92.94, -29.44) * mm, "end": v(92.94, -34.06) * mm});
            skLineSegment(sketch, "E3.15.10.2", {"start": v(97.56, -29.44) * mm, "end": v(97.56, -34.06) * mm});
            skLineSegment(sketch, "E3.15.10.3", {"start": v(92.94, -34.06) * mm, "end": v(97.56, -34.06) * mm});
            skLineSegment(sketch, "E3.15.11.0", {"start": v(92.94, -42.14) * mm, "end": v(97.56, -42.14) * mm});
            skLineSegment(sketch, "E3.15.11.1", {"start": v(92.94, -42.14) * mm, "end": v(92.94, -46.76) * mm});
            skLineSegment(sketch, "E3.15.11.2", {"start": v(97.56, -42.14) * mm, "end": v(97.56, -46.76) * mm});
            skLineSegment(sketch, "E3.15.11.3", {"start": v(92.94, -46.76) * mm, "end": v(97.56, -46.76) * mm});
            skLineSegment(sketch, "E3.15.12.0", {"start": v(92.94, -54.84) * mm, "end": v(97.56, -54.84) * mm});
            skLineSegment(sketch, "E3.15.12.1", {"start": v(92.94, -54.84) * mm, "end": v(92.94, -59.46) * mm});
            skLineSegment(sketch, "E3.15.12.2", {"start": v(97.56, -54.84) * mm, "end": v(97.56, -59.46) * mm});
            skLineSegment(sketch, "E3.15.12.3", {"start": v(92.94, -59.46) * mm, "end": v(97.56, -59.46) * mm});
            skLineSegment(sketch, "E3.15.13.0", {"start": v(92.94, -67.54) * mm, "end": v(97.56, -67.54) * mm});
            skLineSegment(sketch, "E3.15.13.1", {"start": v(92.94, -67.54) * mm, "end": v(92.94, -72.16) * mm});
            skLineSegment(sketch, "E3.15.13.2", {"start": v(97.56, -67.54) * mm, "end": v(97.56, -72.16) * mm});
            skLineSegment(sketch, "E3.15.13.3", {"start": v(92.94, -72.16) * mm, "end": v(97.56, -72.16) * mm});
            skLineSegment(sketch, "E3.15.14.0", {"start": v(92.94, -80.24) * mm, "end": v(97.56, -80.24) * mm});
            skLineSegment(sketch, "E3.15.14.1", {"start": v(92.94, -80.24) * mm, "end": v(92.94, -84.86) * mm});
            skLineSegment(sketch, "E3.15.14.2", {"start": v(97.56, -80.24) * mm, "end": v(97.56, -84.86) * mm});
            skLineSegment(sketch, "E3.15.14.3", {"start": v(92.94, -84.86) * mm, "end": v(97.56, -84.86) * mm});
            skLineSegment(sketch, "E3.15.15.0", {"start": v(92.94, -92.94) * mm, "end": v(97.56, -92.94) * mm});
            skLineSegment(sketch, "E3.15.15.1", {"start": v(92.94, -92.94) * mm, "end": v(92.94, -97.56) * mm});
            skLineSegment(sketch, "E3.15.15.2", {"start": v(97.56, -92.94) * mm, "end": v(97.56, -97.56) * mm});
            skLineSegment(sketch, "E3.15.15.3", {"start": v(92.94, -97.56) * mm, "end": v(97.56, -97.56) * mm});
            skLineSegment(sketch, "E3.15.16.0", {"start": v(92.94, -105.64) * mm, "end": v(97.56, -105.64) * mm});
            skLineSegment(sketch, "E3.15.16.1", {"start": v(92.94, -105.64) * mm, "end": v(92.94, -110.26) * mm});
            skLineSegment(sketch, "E3.15.16.2", {"start": v(97.56, -105.64) * mm, "end": v(97.56, -110.26) * mm});
            skLineSegment(sketch, "E3.15.16.3", {"start": v(92.94, -110.26) * mm, "end": v(97.56, -110.26) * mm});
            skLineSegment(sketch, "E3.16.0.0", {"start": v(105.64, 97.56) * mm, "end": v(110.26, 97.56) * mm});
            skLineSegment(sketch, "E3.16.0.1", {"start": v(105.64, 97.56) * mm, "end": v(105.64, 92.94) * mm});
            skLineSegment(sketch, "E3.16.0.2", {"start": v(110.26, 97.56) * mm, "end": v(110.26, 92.94) * mm});
            skLineSegment(sketch, "E3.16.0.3", {"start": v(105.64, 92.94) * mm, "end": v(110.26, 92.94) * mm});
            skLineSegment(sketch, "E3.16.1.0", {"start": v(105.64, 84.86) * mm, "end": v(110.26, 84.86) * mm});
            skLineSegment(sketch, "E3.16.1.1", {"start": v(105.64, 84.86) * mm, "end": v(105.64, 80.24) * mm});
            skLineSegment(sketch, "E3.16.1.2", {"start": v(110.26, 84.86) * mm, "end": v(110.26, 80.24) * mm});
            skLineSegment(sketch, "E3.16.1.3", {"start": v(105.64, 80.24) * mm, "end": v(110.26, 80.24) * mm});
            skLineSegment(sketch, "E3.16.2.0", {"start": v(105.64, 72.16) * mm, "end": v(110.26, 72.16) * mm});
            skLineSegment(sketch, "E3.16.2.1", {"start": v(105.64, 72.16) * mm, "end": v(105.64, 67.54) * mm});
            skLineSegment(sketch, "E3.16.2.2", {"start": v(110.26, 72.16) * mm, "end": v(110.26, 67.54) * mm});
            skLineSegment(sketch, "E3.16.2.3", {"start": v(105.64, 67.54) * mm, "end": v(110.26, 67.54) * mm});
            skLineSegment(sketch, "E3.16.3.0", {"start": v(105.64, 59.46) * mm, "end": v(110.26, 59.46) * mm});
            skLineSegment(sketch, "E3.16.3.1", {"start": v(105.64, 59.46) * mm, "end": v(105.64, 54.84) * mm});
            skLineSegment(sketch, "E3.16.3.2", {"start": v(110.26, 59.46) * mm, "end": v(110.26, 54.84) * mm});
            skLineSegment(sketch, "E3.16.3.3", {"start": v(105.64, 54.84) * mm, "end": v(110.26, 54.84) * mm});
            skLineSegment(sketch, "E3.16.4.0", {"start": v(105.64, 46.76) * mm, "end": v(110.26, 46.76) * mm});
            skLineSegment(sketch, "E3.16.4.1", {"start": v(105.64, 46.76) * mm, "end": v(105.64, 42.14) * mm});
            skLineSegment(sketch, "E3.16.4.2", {"start": v(110.26, 46.76) * mm, "end": v(110.26, 42.14) * mm});
            skLineSegment(sketch, "E3.16.4.3", {"start": v(105.64, 42.14) * mm, "end": v(110.26, 42.14) * mm});
            skLineSegment(sketch, "E3.16.5.0", {"start": v(105.64, 34.06) * mm, "end": v(110.26, 34.06) * mm});
            skLineSegment(sketch, "E3.16.5.1", {"start": v(105.64, 34.06) * mm, "end": v(105.64, 29.44) * mm});
            skLineSegment(sketch, "E3.16.5.2", {"start": v(110.26, 34.06) * mm, "end": v(110.26, 29.44) * mm});
            skLineSegment(sketch, "E3.16.5.3", {"start": v(105.64, 29.44) * mm, "end": v(110.26, 29.44) * mm});
            skLineSegment(sketch, "E3.16.6.0", {"start": v(105.64, 21.36) * mm, "end": v(110.26, 21.36) * mm});
            skLineSegment(sketch, "E3.16.6.1", {"start": v(105.64, 21.36) * mm, "end": v(105.64, 16.74) * mm});
            skLineSegment(sketch, "E3.16.6.2", {"start": v(110.26, 21.36) * mm, "end": v(110.26, 16.74) * mm});
            skLineSegment(sketch, "E3.16.6.3", {"start": v(105.64, 16.74) * mm, "end": v(110.26, 16.74) * mm});
            skLineSegment(sketch, "E3.16.7.0", {"start": v(105.64, 8.66) * mm, "end": v(110.26, 8.66) * mm});
            skLineSegment(sketch, "E3.16.7.1", {"start": v(105.64, 8.66) * mm, "end": v(105.64, 4.04) * mm});
            skLineSegment(sketch, "E3.16.7.2", {"start": v(110.26, 8.66) * mm, "end": v(110.26, 4.04) * mm});
            skLineSegment(sketch, "E3.16.7.3", {"start": v(105.64, 4.04) * mm, "end": v(110.26, 4.04) * mm});
            skLineSegment(sketch, "E3.16.8.0", {"start": v(105.64, -4.04) * mm, "end": v(110.26, -4.04) * mm});
            skLineSegment(sketch, "E3.16.8.1", {"start": v(105.64, -4.04) * mm, "end": v(105.64, -8.66) * mm});
            skLineSegment(sketch, "E3.16.8.2", {"start": v(110.26, -4.04) * mm, "end": v(110.26, -8.66) * mm});
            skLineSegment(sketch, "E3.16.8.3", {"start": v(105.64, -8.66) * mm, "end": v(110.26, -8.66) * mm});
            skLineSegment(sketch, "E3.16.9.0", {"start": v(105.64, -16.74) * mm, "end": v(110.26, -16.74) * mm});
            skLineSegment(sketch, "E3.16.9.1", {"start": v(105.64, -16.74) * mm, "end": v(105.64, -21.36) * mm});
            skLineSegment(sketch, "E3.16.9.2", {"start": v(110.26, -16.74) * mm, "end": v(110.26, -21.36) * mm});
            skLineSegment(sketch, "E3.16.9.3", {"start": v(105.64, -21.36) * mm, "end": v(110.26, -21.36) * mm});
            skLineSegment(sketch, "E3.16.10.0", {"start": v(105.64, -29.44) * mm, "end": v(110.26, -29.44) * mm});
            skLineSegment(sketch, "E3.16.10.1", {"start": v(105.64, -29.44) * mm, "end": v(105.64, -34.06) * mm});
            skLineSegment(sketch, "E3.16.10.2", {"start": v(110.26, -29.44) * mm, "end": v(110.26, -34.06) * mm});
            skLineSegment(sketch, "E3.16.10.3", {"start": v(105.64, -34.06) * mm, "end": v(110.26, -34.06) * mm});
            skLineSegment(sketch, "E3.16.11.0", {"start": v(105.64, -42.14) * mm, "end": v(110.26, -42.14) * mm});
            skLineSegment(sketch, "E3.16.11.1", {"start": v(105.64, -42.14) * mm, "end": v(105.64, -46.76) * mm});
            skLineSegment(sketch, "E3.16.11.2", {"start": v(110.26, -42.14) * mm, "end": v(110.26, -46.76) * mm});
            skLineSegment(sketch, "E3.16.11.3", {"start": v(105.64, -46.76) * mm, "end": v(110.26, -46.76) * mm});
            skLineSegment(sketch, "E3.16.12.0", {"start": v(105.64, -54.84) * mm, "end": v(110.26, -54.84) * mm});
            skLineSegment(sketch, "E3.16.12.1", {"start": v(105.64, -54.84) * mm, "end": v(105.64, -59.46) * mm});
            skLineSegment(sketch, "E3.16.12.2", {"start": v(110.26, -54.84) * mm, "end": v(110.26, -59.46) * mm});
            skLineSegment(sketch, "E3.16.12.3", {"start": v(105.64, -59.46) * mm, "end": v(110.26, -59.46) * mm});
            skLineSegment(sketch, "E3.16.13.0", {"start": v(105.64, -67.54) * mm, "end": v(110.26, -67.54) * mm});
            skLineSegment(sketch, "E3.16.13.1", {"start": v(105.64, -67.54) * mm, "end": v(105.64, -72.16) * mm});
            skLineSegment(sketch, "E3.16.13.2", {"start": v(110.26, -67.54) * mm, "end": v(110.26, -72.16) * mm});
            skLineSegment(sketch, "E3.16.13.3", {"start": v(105.64, -72.16) * mm, "end": v(110.26, -72.16) * mm});
            skLineSegment(sketch, "E3.16.14.0", {"start": v(105.64, -80.24) * mm, "end": v(110.26, -80.24) * mm});
            skLineSegment(sketch, "E3.16.14.1", {"start": v(105.64, -80.24) * mm, "end": v(105.64, -84.86) * mm});
            skLineSegment(sketch, "E3.16.14.2", {"start": v(110.26, -80.24) * mm, "end": v(110.26, -84.86) * mm});
            skLineSegment(sketch, "E3.16.14.3", {"start": v(105.64, -84.86) * mm, "end": v(110.26, -84.86) * mm});
            skLineSegment(sketch, "E3.16.15.0", {"start": v(105.64, -92.94) * mm, "end": v(110.26, -92.94) * mm});
            skLineSegment(sketch, "E3.16.15.1", {"start": v(105.64, -92.94) * mm, "end": v(105.64, -97.56) * mm});
            skLineSegment(sketch, "E3.16.15.2", {"start": v(110.26, -92.94) * mm, "end": v(110.26, -97.56) * mm});
            skLineSegment(sketch, "E3.16.15.3", {"start": v(105.64, -97.56) * mm, "end": v(110.26, -97.56) * mm});
            skLineSegment(sketch, "E3.16.16.0", {"start": v(105.64, -105.64) * mm, "end": v(110.26, -105.64) * mm});
            skLineSegment(sketch, "E3.16.16.1", {"start": v(105.64, -105.64) * mm, "end": v(105.64, -110.26) * mm});
            skLineSegment(sketch, "E3.16.16.2", {"start": v(110.26, -105.64) * mm, "end": v(110.26, -110.26) * mm});
            skLineSegment(sketch, "E3.16.16.3", {"start": v(105.64, -110.26) * mm, "end": v(110.26, -110.26) * mm});
            skLineSegment(sketch, "E3.direction1", {"start": v(-97.56, 97.56) * mm, "end": v(-84.86, 97.56) * mm, "construction": true});
            skLineSegment(sketch, "E3.direction2", {"start": v(-97.56, 97.56) * mm, "end": v(-97.56, 84.86) * mm, "construction": true});
            skLineSegment(sketch, "E4.bottom", {"start": v(-101.6, 101.6) * mm, "end": v(-38.1, 101.6) * mm});
            skLineSegment(sketch, "E4.top", {"start": v(-101.6, -114.3) * mm, "end": v(-38.1, -114.3) * mm});
            skLineSegment(sketch, "E4.left", {"start": v(-101.6, 101.6) * mm, "end": v(-101.6, 38.1) * mm});
            skLineSegment(sketch, "E4.right", {"start": v(114.3, 101.6) * mm, "end": v(114.3, 38.1) * mm});
            skPoint(sketch, "E0.top.start.orphan", {"position": v(101.6, -101.6) * mm});
            skLineSegment(sketch, "E5", {"start": v(50.8, -114.3) * mm, "end": v(50.8, -76.2) * mm});
            skLineSegment(sketch, "E6.bottom", {"start": v(50.8, -76.2) * mm, "end": v(-38.1, -76.2) * mm});
            skLineSegment(sketch, "E6.left", {"start": v(50.8, -76.2) * mm, "end": v(50.8, -114.3) * mm});
            skLineSegment(sketch, "E6.right", {"start": v(-38.1, -76.2) * mm, "end": v(-38.1, -114.3) * mm});
            skPoint(sketch, "E7.start.orphan", {"position": v(6.35, -114.3) * mm});
            skLineSegment(sketch, "E8.trimOffspring", {"start": v(50.8, -114.3) * mm, "end": v(114.3, -114.3) * mm});
            skLineSegment(sketch, "E9", {"start": v(50.8, 101.6) * mm, "end": v(50.8, 63.5) * mm});
            skLineSegment(sketch, "E10", {"start": v(50.8, 63.5) * mm, "end": v(-38.1, 63.5) * mm});
            skLineSegment(sketch, "E11", {"start": v(-38.1, 63.5) * mm, "end": v(-38.1, 101.6) * mm});
            skLineSegment(sketch, "E12.trimOffspring", {"start": v(101.6, 101.6) * mm, "end": v(114.3, 101.6) * mm});
            skPoint(sketch, "E13.orphan", {"position": v(6.35, 101.6) * mm});
            skLineSegment(sketch, "E14.trimOffspring", {"start": v(-38.1, 101.6) * mm, "end": v(-101.6, 101.6) * mm});
            skLineSegment(sketch, "E15", {"start": v(114.3, 38.1) * mm, "end": v(76.2, 38.1) * mm});
            skLineSegment(sketch, "E16", {"start": v(76.2, 38.1) * mm, "end": v(76.2, -50.8) * mm});
            skLineSegment(sketch, "E17", {"start": v(76.2, -50.8) * mm, "end": v(114.3, -50.8) * mm});
            skPoint(sketch, "E18.start.orphan", {"position": v(114.3, -6.35) * mm});
            skLineSegment(sketch, "E19.trimOffspring", {"start": v(114.3, -50.8) * mm, "end": v(114.3, -114.3) * mm});
            skLineSegment(sketch, "E20", {"start": v(-101.6, 38.1) * mm, "end": v(-63.5, 38.1) * mm});
            skLineSegment(sketch, "E21", {"start": v(-63.5, 38.1) * mm, "end": v(-63.5, -50.8) * mm});
            skLineSegment(sketch, "E22", {"start": v(-63.5, -50.8) * mm, "end": v(-101.6, -50.8) * mm});
            skPoint(sketch, "E23.orphan", {"position": v(-101.6, -6.35) * mm});
            skPoint(sketch, "E24.trimOffspring.end.orphan", {"position": v(-101.6, -101.6) * mm});
            skLineSegment(sketch, "E25.trimOffspring", {"start": v(-101.6, -50.8) * mm, "end": v(-101.6, -114.3) * mm});
            skSolve(sketch);
        }
        {
            var Q0;
            Q0=makeQuery(id+"F0.imprint","IMPRINT",FACE,{"disambiguationData":[TD([[makeQuery(id+"F0.imprint","IMPRINT",EDGE,{"derivedFrom":sQuery(id+"F0.wireOp",EDGE,"E0.bottom")}),1.0]])]});
            extrude(context, id + "F1", {"entities" : qUnion([Q0]), "depth" : 1 / 203.2 * mm});
        }
    });
